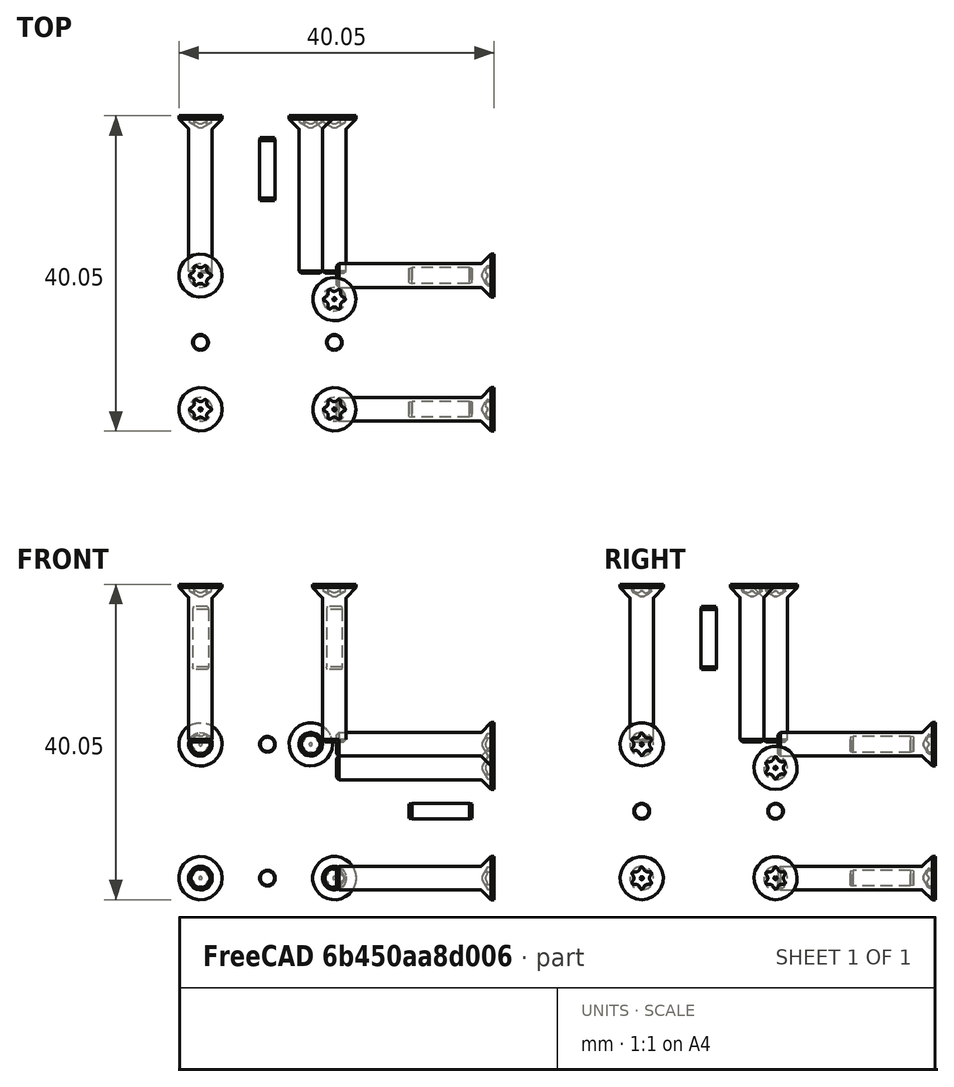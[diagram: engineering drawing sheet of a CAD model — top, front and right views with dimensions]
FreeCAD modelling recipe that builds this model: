
FCSTD DOCUMENT  (FreeCAD 1.2R45225 (Git))
Label: Assembly_MicroManipulator
License: All rights reserved
LicenseURL: https://en.wikipedia.org/wiki/All_rights_reserved
objects: App::Link×125, Part::FeaturePython×18, App::Point×13, Assembly::AssemblyLink×12, App::FeaturePython×4, Assembly::JointGroup×1, App::DocumentObjectGroup×1, Assembly::AssemblyObject×1
note: 18 computed .brp shape members not serialized (recipe doc carries the construction recipe); baked Part::Feature solids carry a one-line shape summary decoded from their .brp
EXTERNAL_REF file=BaseBlock.FCStd obj=Body
EXTERNAL_REF file=EndEffector.FCStd obj=Body
EXTERNAL_REF file=Assembly_Actuator.FCStd obj=Assembly
EXTERNAL_REF file=Assembly_Actuator.FCStd obj=MotorMount
EXTERNAL_REF file=Assembly_Actuator.FCStd obj=StepperMotorNema17
EXTERNAL_REF file=Assembly_Actuator.FCStd obj=MotorHorn
EXTERNAL_REF file=Assembly_Actuator.FCStd obj=LinkageUnit
EXTERNAL_REF file=Assembly_LinkageUnit.FCStd obj=LinkageRod
EXTERNAL_REF file=Assembly_LinkageUnit.FCStd obj=LinkageRod001
EXTERNAL_REF file=Assembly_LinkageUnit.FCStd obj=RubberBandCollet001
EXTERNAL_REF file=Assembly_LinkageUnit.FCStd obj=RubberBandCollet
EXTERNAL_REF file=Assembly_LinkageUnit.FCStd obj=RubberBandCollet002
EXTERNAL_REF file=Assembly_LinkageUnit.FCStd obj=RubberBandCollet003
EXTERNAL_REF file=Assembly_Actuator.FCStd obj=EncoderMAgnetArray
EXTERNAL_REF file=Assembly_Actuator.FCStd obj=MT6835
EXTERNAL_REF file=Assembly_Actuator.FCStd obj=Screw
EXTERNAL_REF file=Assembly_Actuator.FCStd obj=Screw001
EXTERNAL_REF file=Assembly_Actuator.FCStd obj=Screw002
EXTERNAL_REF file=Assembly_Actuator.FCStd obj=Screw003
EXTERNAL_REF file=Assembly_Actuator.FCStd obj=Pin
EXTERNAL_REF file=Assembly_Actuator.FCStd obj=Pin001
EXTERNAL_REF file=Assembly_Actuator.FCStd obj=Screw004
EXTERNAL_REF file=Assembly_Actuator.FCStd obj=Screw005
EXTERNAL_REF file=Assembly_Actuator.FCStd obj=Screw006
EXTERNAL_REF file=Assembly_Actuator.FCStd obj=Pin002
EXTERNAL_REF file=Assembly_Actuator.FCStd obj=Screw007
EXTERNAL_REF file=Assembly_Actuator.FCStd obj=Screw008
EXTERNAL_REF file=Assembly_LinkageUnit.FCStd obj=BallJointPlateAsm
EXTERNAL_REF file=Assembly_BallJointPlate.FCStd obj=BallJointPlate
EXTERNAL_REF file=Assembly_BallJointPlate.FCStd obj=Ball
EXTERNAL_REF file=Assembly_BallJointPlate.FCStd obj=Ball001
EXTERNAL_REF file=Assembly_BallJointPlate.FCStd obj=RubberBand
EXTERNAL_REF file=Assembly_BallJointPlate.FCStd obj=RubberBand001
EXTERNAL_REF file=Assembly_BallJointPlate.FCStd obj=CrimpBead
EXTERNAL_REF file=Assembly_BallJointPlate.FCStd obj=CrimpBead001
EXTERNAL_REF file=Assembly_BallJointPlate.FCStd obj=CrimpBead002
EXTERNAL_REF file=Assembly_BallJointPlate.FCStd obj=CrimpBead003
EXTERNAL_REF file=Assembly_LinkageUnit.FCStd obj=BallJointPlateAsm001

FEATURE [App::Point] Origin001
  Role = Origin
FEATURE [App::Link] BaseBlock
  LinkedObject = -> <external BaseBlock.FCStd>#Body
FEATURE [App::Link] Endeffector
  LinkPlacement = pos=(47.5,47.5,47.5) rot=(0,0,1;0rad)
  LinkedObject = -> <external EndEffector.FCStd>#Body
  Placement = pos=(47.5,47.5,47.5) rot=(0,0,1;0rad)
FEATURE [App::Point] Origin009
  Role = Origin
FEATURE [App::Link] MotorMount
  LinkPlacement = pos=(0,0,-10.5) rot=(0.707107,0.707107,0;3.14159rad)
  LinkedObject = -> <external Assembly_Actuator.FCStd>#MotorMount
  Placement = pos=(0,0,-10.5) rot=(0.707107,0.707107,0;3.14159rad)
FEATURE [App::Link] StepperMotorNema003
  LinkPlacement = pos=(1.13144e-05,-3.1139e-06,-55.5) rot=(0,0,1;1.5708rad)
  LinkedObject = -> <external Assembly_Actuator.FCStd>#StepperMotorNema17
  Placement = pos=(1.13144e-05,-3.1139e-06,-55.5) rot=(0,0,1;1.5708rad)
FEATURE [App::Link] MotorHorn003
  LinkPlacement = pos=(8.34465e-06,1.54972e-05,-10) rot=(0,0,1;0rad)
  LinkedObject = -> <external Assembly_Actuator.FCStd>#MotorHorn
  Placement = pos=(8.34465e-06,1.54972e-05,-10) rot=(0,0,1;0rad)
FEATURE [App::Point] Origin011  label="Origin012"
  Role = Origin
FEATURE [App::Link] LinkageRod  label="LinkageRod1"
  LinkPlacement = pos=(8.5,0,0) rot=(0,0,1;0rad)
  LinkedObject = -> <external Assembly_LinkageUnit.FCStd>#LinkageRod
  Placement = pos=(8.5,0,0) rot=(0,0,1;0rad)
FEATURE [App::Link] LinkageRod001  label="LinkageRod2"
  LinkPlacement = pos=(-8.5,0,0) rot=(0,0,1;0rad)
  LinkedObject = -> <external Assembly_LinkageUnit.FCStd>#LinkageRod001
  Placement = pos=(-8.5,0,0) rot=(0,0,1;0rad)
FEATURE [App::Link] RubberBandCollet012
  LinkPlacement = pos=(-8.5,24.5,5.51344e-07) rot=(0,0.707107,0.707107;3.14159rad)
  LinkedObject = -> <external Assembly_LinkageUnit.FCStd>#RubberBandCollet001
  Placement = pos=(-8.5,24.5,5.51344e-07) rot=(0,0.707107,0.707107;3.14159rad)
FEATURE [App::Link] RubberBandCollet013
  LinkPlacement = pos=(8.5,24.5,4.02331e-07) rot=(0,0.707107,0.707107;3.14159rad)
  LinkedObject = -> <external Assembly_LinkageUnit.FCStd>#RubberBandCollet
  Placement = pos=(8.5,24.5,4.02331e-07) rot=(0,0.707107,0.707107;3.14159rad)
FEATURE [App::Link] RubberBandCollet014
  LinkPlacement = pos=(-8.5,-24.5,-1.1921e-07) rot=(1,0,0;1.5708rad)
  LinkedObject = -> <external Assembly_LinkageUnit.FCStd>#RubberBandCollet002
  Placement = pos=(-8.5,-24.5,-1.1921e-07) rot=(1,0,0;1.5708rad)
FEATURE [App::Link] RubberBandCollet015
  LinkPlacement = pos=(8.5,-24.5,9.98377e-07) rot=(-1,0,0;1.5708rad)
  LinkedObject = -> <external Assembly_LinkageUnit.FCStd>#RubberBandCollet003
  Placement = pos=(8.5,-24.5,9.98377e-07) rot=(-1,0,0;1.5708rad)
FEATURE [App::Link] EncoderMAgnetArray003  label="EncoderMagnetArray"
  LinkPlacement = pos=(9.53674e-07,9.23872e-07,-8.00001) rot=(0,0,1;0rad)
  LinkedObject = -> <external Assembly_Actuator.FCStd>#EncoderMAgnetArray
  Placement = pos=(9.53674e-07,9.23872e-07,-8.00001) rot=(0,0,1;0rad)
FEATURE [App::Link] MT6838
  LinkPlacement = pos=(-32.5,1.41501e-05,-10) rot=(0,1,0;1.5708rad)
  LinkedObject = -> <external Assembly_Actuator.FCStd>#MT6835
  Placement = pos=(-32.5,1.41501e-05,-10) rot=(0,1,0;1.5708rad)
FEATURE [App::Link] Screw  label="M3x10-Screw"
  LinkPlacement = pos=(15.5,15.5,-10.5) rot=(1.0625,0,0;0rad)
  LinkedObject = -> <external Assembly_Actuator.FCStd>#Screw
  Placement = pos=(15.5,15.5,-10.5) rot=(1.0625,0,0;0rad)
FEATURE [App::Link] Screw001  label="M3x10-Screw008"
  LinkPlacement = pos=(-15.5,15.5,-10.5) rot=(1.0625,0,0;0rad)
  LinkedObject = -> <external Assembly_Actuator.FCStd>#Screw001
  Placement = pos=(-15.5,15.5,-10.5) rot=(1.0625,0,0;0rad)
FEATURE [App::Link] Screw002  label="M3x10-Screw009"
  LinkPlacement = pos=(-15.5,-15.5,-10.5) rot=(1.0625,0,0;0rad)
  LinkedObject = -> <external Assembly_Actuator.FCStd>#Screw002
  Placement = pos=(-15.5,-15.5,-10.5) rot=(1.0625,0,0;0rad)
FEATURE [App::Link] Screw003  label="M3x6-Screw"
  LinkPlacement = pos=(15.5,-15.5,-14.5) rot=(1.0625,0,0;0rad)
  LinkedObject = -> <external Assembly_Actuator.FCStd>#Screw003
  Placement = pos=(15.5,-15.5,-14.5) rot=(1.0625,0,0;0rad)
FEATURE [App::Link] Pin  label="2 mmx8-Pin"
  LinkPlacement = pos=(12,0.299999,4.75) rot=(1,0,0;1.5708rad)
  LinkedObject = -> <external Assembly_Actuator.FCStd>#Pin
  Placement = pos=(12,0.299999,4.75) rot=(1,0,0;1.5708rad)
FEATURE [App::Link] Pin001  label="2 mmx8-Pin004"
  LinkPlacement = pos=(12,0.300001,-4.75) rot=(1,0,0;1.5708rad)
  LinkedObject = -> <external Assembly_Actuator.FCStd>#Pin001
  Placement = pos=(12,0.300001,-4.75) rot=(1,0,0;1.5708rad)
FEATURE [App::Link] Screw004  label="M2x8-Screw"
  LinkPlacement = pos=(15,0.299999,4.75) rot=(1,0,0;1.5708rad)
  LinkedObject = -> <external Assembly_Actuator.FCStd>#Screw004
  Placement = pos=(15,0.299999,4.75) rot=(1,0,0;1.5708rad)
FEATURE [App::Link] Screw005  label="M2x8-Screw005"
  LinkPlacement = pos=(15,0.300001,-4.75) rot=(1,0,0;1.5708rad)
  LinkedObject = -> <external Assembly_Actuator.FCStd>#Screw005
  Placement = pos=(15,0.300001,-4.75) rot=(1,0,0;1.5708rad)
FEATURE [App::Link] Screw006  label="M2x8-Screw004"
  LinkPlacement = pos=(-34.1,1.41501e-05,-16) rot=(0,-1,0;1.5708rad)
  LinkedObject = -> <external Assembly_Actuator.FCStd>#Screw006
  Placement = pos=(-34.1,1.41501e-05,-16) rot=(0,-1,0;1.5708rad)
FEATURE [App::FeaturePython] GroundedJoint  # Assembly grounded joint (typed FeaturePython)
  ObjectToGround = -> BaseBlock
FEATURE [App::FeaturePython] Joint  label="Fixed1"  # Assembly joint (typed FeaturePython)
  Angle = 0
  AngleMax = 0
  AngleMin = 0
  Detach1 = false
  Detach2 = false
  Distance = 0
  Distance2 = 0
  EnableAngleMax = false
  EnableAngleMin = false
  EnableLengthMax = false
  EnableLengthMin = false
  JointType = 0 (Fixed)
  LengthMax = 0
  LengthMin = 0
  Offset2 = pos=(-21,-21.5,-52) rot=(0,0,-1;1.5708rad)
  Placement2 = pos=(-21,-21.5,-52) rot=(0,0,-1;1.5708rad)
  Reference1 = -> BaseBlock
  Reference2 = -> Actuator
  Suppressed = false
FEATURE [App::Point] Origin013  label="Origin015"
  Role = Origin
FEATURE [App::Link] MotorMount001
  LinkPlacement = pos=(0,0,-10.5) rot=(0.707107,0.707107,0;3.14159rad)
  LinkedObject = -> <external Assembly_Actuator.FCStd>#MotorMount
  Placement = pos=(0,0,-10.5) rot=(0.707107,0.707107,0;3.14159rad)
FEATURE [App::Link] StepperMotorNema004
  LinkPlacement = pos=(1.13144e-05,-3.1139e-06,-55.5) rot=(0,0,1;1.5708rad)
  LinkedObject = -> <external Assembly_Actuator.FCStd>#StepperMotorNema17
  Placement = pos=(1.13144e-05,-3.1139e-06,-55.5) rot=(0,0,1;1.5708rad)
FEATURE [App::Link] MotorHorn004
  LinkPlacement = pos=(8.34465e-06,1.54972e-05,-10) rot=(0,0,1;0rad)
  LinkedObject = -> <external Assembly_Actuator.FCStd>#MotorHorn
  Placement = pos=(8.34465e-06,1.54972e-05,-10) rot=(0,0,1;0rad)
FEATURE [App::Point] Origin015  label="Origin017"
  Role = Origin
FEATURE [App::Link] LinkageRod002  label="LinkageRod001"
  LinkPlacement = pos=(8.5,0,0) rot=(0,0,1;0rad)
  LinkedObject = -> <external Assembly_LinkageUnit.FCStd>#LinkageRod
  Placement = pos=(8.5,0,0) rot=(0,0,1;0rad)
FEATURE [App::Link] LinkageRod003  label="LinkageRod002"
  LinkPlacement = pos=(-8.5,0,0) rot=(0,0,1;0rad)
  LinkedObject = -> <external Assembly_LinkageUnit.FCStd>#LinkageRod001
  Placement = pos=(-8.5,0,0) rot=(0,0,1;0rad)
FEATURE [App::Link] RubberBandCollet016
  LinkPlacement = pos=(-8.5,24.5,5.51344e-07) rot=(0,0.707107,0.707107;3.14159rad)
  LinkedObject = -> <external Assembly_LinkageUnit.FCStd>#RubberBandCollet001
  Placement = pos=(-8.5,24.5,5.51344e-07) rot=(0,0.707107,0.707107;3.14159rad)
FEATURE [App::Link] RubberBandCollet017
  LinkPlacement = pos=(8.5,24.5,4.02331e-07) rot=(0,0.707107,0.707107;3.14159rad)
  LinkedObject = -> <external Assembly_LinkageUnit.FCStd>#RubberBandCollet
  Placement = pos=(8.5,24.5,4.02331e-07) rot=(0,0.707107,0.707107;3.14159rad)
FEATURE [App::Link] RubberBandCollet018
  LinkPlacement = pos=(-8.5,-24.5,-1.1921e-07) rot=(1,0,0;1.5708rad)
  LinkedObject = -> <external Assembly_LinkageUnit.FCStd>#RubberBandCollet002
  Placement = pos=(-8.5,-24.5,-1.1921e-07) rot=(1,0,0;1.5708rad)
FEATURE [App::Link] RubberBandCollet019
  LinkPlacement = pos=(8.5,-24.5,9.98377e-07) rot=(-1,0,0;1.5708rad)
  LinkedObject = -> <external Assembly_LinkageUnit.FCStd>#RubberBandCollet003
  Placement = pos=(8.5,-24.5,9.98377e-07) rot=(-1,0,0;1.5708rad)
FEATURE [App::Link] EncoderMAgnetArray004  label="EncoderMagnetArray001"
  LinkPlacement = pos=(9.53674e-07,9.23872e-07,-8.00001) rot=(0,0,1;0rad)
  LinkedObject = -> <external Assembly_Actuator.FCStd>#EncoderMAgnetArray
  Placement = pos=(9.53674e-07,9.23872e-07,-8.00001) rot=(0,0,1;0rad)
FEATURE [App::Link] MT6839
  LinkPlacement = pos=(-32.5,1.41501e-05,-10) rot=(0,1,0;1.5708rad)
  LinkedObject = -> <external Assembly_Actuator.FCStd>#MT6835
  Placement = pos=(-32.5,1.41501e-05,-10) rot=(0,1,0;1.5708rad)
FEATURE [App::Link] Screw007  label="M3x10-Screw010"
  LinkPlacement = pos=(15.5,15.5,-10.5) rot=(1.0625,0,0;0rad)
  LinkedObject = -> <external Assembly_Actuator.FCStd>#Screw
  Placement = pos=(15.5,15.5,-10.5) rot=(1.0625,0,0;0rad)
FEATURE [App::Link] Screw008  label="M3x10-Screw011"
  LinkPlacement = pos=(-15.5,15.5,-10.5) rot=(1.0625,0,0;0rad)
  LinkedObject = -> <external Assembly_Actuator.FCStd>#Screw001
  Placement = pos=(-15.5,15.5,-10.5) rot=(1.0625,0,0;0rad)
FEATURE [App::Link] Screw009  label="M3x10-Screw012"
  LinkPlacement = pos=(-15.5,-15.5,-10.5) rot=(1.0625,0,0;0rad)
  LinkedObject = -> <external Assembly_Actuator.FCStd>#Screw002
  Placement = pos=(-15.5,-15.5,-10.5) rot=(1.0625,0,0;0rad)
FEATURE [App::Link] Screw010  label="M3x6-Screw001"
  LinkPlacement = pos=(15.5,-15.5,-14.5) rot=(1.0625,0,0;0rad)
  LinkedObject = -> <external Assembly_Actuator.FCStd>#Screw003
  Placement = pos=(15.5,-15.5,-14.5) rot=(1.0625,0,0;0rad)
FEATURE [App::Link] Pin002  label="2 mmx8-Pin005"
  LinkPlacement = pos=(12,0.299999,4.75) rot=(1,0,0;1.5708rad)
  LinkedObject = -> <external Assembly_Actuator.FCStd>#Pin
  Placement = pos=(12,0.299999,4.75) rot=(1,0,0;1.5708rad)
FEATURE [App::Link] Pin003  label="2 mmx8-Pin006"
  LinkPlacement = pos=(12,0.300001,-4.75) rot=(1,0,0;1.5708rad)
  LinkedObject = -> <external Assembly_Actuator.FCStd>#Pin001
  Placement = pos=(12,0.300001,-4.75) rot=(1,0,0;1.5708rad)
FEATURE [App::Link] Screw011  label="M2x8-Screw006"
  LinkPlacement = pos=(15,0.299999,4.75) rot=(1,0,0;1.5708rad)
  LinkedObject = -> <external Assembly_Actuator.FCStd>#Screw004
  Placement = pos=(15,0.299999,4.75) rot=(1,0,0;1.5708rad)
FEATURE [App::Link] Screw012  label="M2x8-Screw007"
  LinkPlacement = pos=(15,0.300001,-4.75) rot=(1,0,0;1.5708rad)
  LinkedObject = -> <external Assembly_Actuator.FCStd>#Screw005
  Placement = pos=(15,0.300001,-4.75) rot=(1,0,0;1.5708rad)
FEATURE [App::Link] Screw013  label="M2x8-Screw008"
  LinkPlacement = pos=(-34.1,1.41501e-05,-16) rot=(0,-1,0;1.5708rad)
  LinkedObject = -> <external Assembly_Actuator.FCStd>#Screw006
  Placement = pos=(-34.1,1.41501e-05,-16) rot=(0,-1,0;1.5708rad)
FEATURE [App::FeaturePython] Joint001  label="Fixed2"  # Assembly joint (typed FeaturePython)
  Angle = 0
  AngleMax = 0
  AngleMin = 0
  Detach1 = false
  Detach2 = false
  Distance = 0
  Distance2 = 0
  EnableAngleMax = false
  EnableAngleMin = false
  EnableLengthMax = false
  EnableLengthMin = false
  JointType = 0 (Fixed)
  LengthMax = 0
  LengthMin = 0
  Offset2 = pos=(-21,-21.5,-52) rot=(0.707107,0,0.707107;3.14159rad)
  Placement2 = pos=(-21,-21.5,-52) rot=(0.707107,0,0.707107;3.14159rad)
  Reference1 = -> BaseBlock
  Reference2 = -> Actuator001
  Suppressed = false
FEATURE [App::Point] Origin017  label="Origin020"
  Role = Origin
FEATURE [App::Link] MotorMount002
  LinkPlacement = pos=(0,0,-10.5) rot=(0.707107,0.707107,0;3.14159rad)
  LinkedObject = -> <external Assembly_Actuator.FCStd>#MotorMount
  Placement = pos=(0,0,-10.5) rot=(0.707107,0.707107,0;3.14159rad)
FEATURE [App::Link] StepperMotorNema17
  LinkPlacement = pos=(1.13144e-05,-3.1139e-06,-55.5) rot=(0,0,1;1.5708rad)
  LinkedObject = -> <external Assembly_Actuator.FCStd>#StepperMotorNema17
  Placement = pos=(1.13144e-05,-3.1139e-06,-55.5) rot=(0,0,1;1.5708rad)
FEATURE [App::Link] MotorHorn
  LinkPlacement = pos=(8.34465e-06,1.54972e-05,-10) rot=(0,0,1;0rad)
  LinkedObject = -> <external Assembly_Actuator.FCStd>#MotorHorn
  Placement = pos=(8.34465e-06,1.54972e-05,-10) rot=(0,0,1;0rad)
FEATURE [App::Point] Origin019  label="Origin023"
  Role = Origin
FEATURE [App::Link] LinkageRod004  label="LinkageRod003"
  LinkPlacement = pos=(8.5,0,0) rot=(0,0,1;0rad)
  LinkedObject = -> <external Assembly_LinkageUnit.FCStd>#LinkageRod
  Placement = pos=(8.5,0,0) rot=(0,0,1;0rad)
FEATURE [App::Link] LinkageRod005  label="LinkageRod004"
  LinkPlacement = pos=(-8.5,0,0) rot=(0,0,1;0rad)
  LinkedObject = -> <external Assembly_LinkageUnit.FCStd>#LinkageRod001
  Placement = pos=(-8.5,0,0) rot=(0,0,1;0rad)
FEATURE [App::Link] RubberBandCollet001  label="RubberBandCollet1"
  LinkPlacement = pos=(-8.5,24.5,5.51344e-07) rot=(0,0.707107,0.707107;3.14159rad)
  LinkedObject = -> <external Assembly_LinkageUnit.FCStd>#RubberBandCollet001
  Placement = pos=(-8.5,24.5,5.51344e-07) rot=(0,0.707107,0.707107;3.14159rad)
FEATURE [App::Link] RubberBandCollet  label="RubberBandCollet2"
  LinkPlacement = pos=(8.5,24.5,4.02331e-07) rot=(0,0.707107,0.707107;3.14159rad)
  LinkedObject = -> <external Assembly_LinkageUnit.FCStd>#RubberBandCollet
  Placement = pos=(8.5,24.5,4.02331e-07) rot=(0,0.707107,0.707107;3.14159rad)
FEATURE [App::Link] RubberBandCollet002  label="RubberBandCollet3"
  LinkPlacement = pos=(-8.5,-24.5,-1.1921e-07) rot=(1,0,0;1.5708rad)
  LinkedObject = -> <external Assembly_LinkageUnit.FCStd>#RubberBandCollet002
  Placement = pos=(-8.5,-24.5,-1.1921e-07) rot=(1,0,0;1.5708rad)
FEATURE [App::Link] RubberBandCollet003  label="RubberBandCollet4"
  LinkPlacement = pos=(8.5,-24.5,9.98377e-07) rot=(-1,0,0;1.5708rad)
  LinkedObject = -> <external Assembly_LinkageUnit.FCStd>#RubberBandCollet003
  Placement = pos=(8.5,-24.5,9.98377e-07) rot=(-1,0,0;1.5708rad)
FEATURE [App::Link] EncoderMAgnetArray  label="EncoderMagnetArray002"
  LinkPlacement = pos=(9.53674e-07,9.23872e-07,-8.00001) rot=(0,0,1;0rad)
  LinkedObject = -> <external Assembly_Actuator.FCStd>#EncoderMAgnetArray
  Placement = pos=(9.53674e-07,9.23872e-07,-8.00001) rot=(0,0,1;0rad)
FEATURE [App::Link] MT6835
  LinkPlacement = pos=(-32.5,1.41501e-05,-10) rot=(0,1,0;1.5708rad)
  LinkedObject = -> <external Assembly_Actuator.FCStd>#MT6835
  Placement = pos=(-32.5,1.41501e-05,-10) rot=(0,1,0;1.5708rad)
FEATURE [App::Link] Screw014  label="M3x10-Screw013"
  LinkPlacement = pos=(15.5,15.5,-10.5) rot=(1.0625,0,0;0rad)
  LinkedObject = -> <external Assembly_Actuator.FCStd>#Screw
  Placement = pos=(15.5,15.5,-10.5) rot=(1.0625,0,0;0rad)
FEATURE [App::Link] Screw015  label="M3x10-Screw014"
  LinkPlacement = pos=(-15.5,15.5,-10.5) rot=(1.0625,0,0;0rad)
  LinkedObject = -> <external Assembly_Actuator.FCStd>#Screw001
  Placement = pos=(-15.5,15.5,-10.5) rot=(1.0625,0,0;0rad)
FEATURE [App::Link] Screw016  label="M3x10-Screw015"
  LinkPlacement = pos=(-15.5,-15.5,-10.5) rot=(1.0625,0,0;0rad)
  LinkedObject = -> <external Assembly_Actuator.FCStd>#Screw002
  Placement = pos=(-15.5,-15.5,-10.5) rot=(1.0625,0,0;0rad)
FEATURE [App::Link] Screw017  label="M3x6-Screw002"
  LinkPlacement = pos=(15.5,-15.5,-14.5) rot=(1.0625,0,0;0rad)
  LinkedObject = -> <external Assembly_Actuator.FCStd>#Screw003
  Placement = pos=(15.5,-15.5,-14.5) rot=(1.0625,0,0;0rad)
FEATURE [App::Link] Pin004  label="2 mmx8-Pin007"
  LinkPlacement = pos=(12,0.299999,4.75) rot=(1,0,0;1.5708rad)
  LinkedObject = -> <external Assembly_Actuator.FCStd>#Pin
  Placement = pos=(12,0.299999,4.75) rot=(1,0,0;1.5708rad)
FEATURE [App::Link] Pin005  label="2 mmx8-Pin008"
  LinkPlacement = pos=(12,0.300001,-4.75) rot=(1,0,0;1.5708rad)
  LinkedObject = -> <external Assembly_Actuator.FCStd>#Pin001
  Placement = pos=(12,0.300001,-4.75) rot=(1,0,0;1.5708rad)
FEATURE [App::Link] Screw018  label="M2x8-Screw009"
  LinkPlacement = pos=(15,0.299999,4.75) rot=(1,0,0;1.5708rad)
  LinkedObject = -> <external Assembly_Actuator.FCStd>#Screw004
  Placement = pos=(15,0.299999,4.75) rot=(1,0,0;1.5708rad)
FEATURE [App::Link] Screw019  label="M2x8-Screw010"
  LinkPlacement = pos=(15,0.300001,-4.75) rot=(1,0,0;1.5708rad)
  LinkedObject = -> <external Assembly_Actuator.FCStd>#Screw005
  Placement = pos=(15,0.300001,-4.75) rot=(1,0,0;1.5708rad)
FEATURE [App::Link] Screw020  label="M2x8-Screw011"
  LinkPlacement = pos=(-34.1,1.41501e-05,-16) rot=(0,-1,0;1.5708rad)
  LinkedObject = -> <external Assembly_Actuator.FCStd>#Screw006
  Placement = pos=(-34.1,1.41501e-05,-16) rot=(0,-1,0;1.5708rad)
FEATURE [App::FeaturePython] Joint002  label="Fixed3"  # Assembly joint (typed FeaturePython)
  Angle = 0
  AngleMax = 0
  AngleMin = 0
  Detach1 = false
  Detach2 = false
  Distance = 0
  Distance2 = 0
  EnableAngleMax = false
  EnableAngleMin = false
  EnableLengthMax = false
  EnableLengthMin = false
  JointType = 0 (Fixed)
  LengthMax = 0
  LengthMin = 0
  Offset2 = pos=(-21,-21.5,-52) rot=(1,0,0;1.5708rad)
  Placement2 = pos=(-21,-21.5,-52) rot=(1,0,0;1.5708rad)
  Reference1 = -> BaseBlock
  Reference2 = -> Actuator002
  Suppressed = false
FEATURE [Assembly::JointGroup] Joints
  Group = -> [GroundedJoint,Joint,Joint001,Joint002]
FEATURE [Part::FeaturePython] Screw021  label="M3x20-Screw"  # WARN: FeaturePython — macro-defined, semantics opaque (R4)
  BaseObject = -> Actuator [MotorMount.Fillet020.Edge283]
  Diameter = 3
  Invert = false
  LeftHanded = false
  Length = 5
  LengthCustom = 20
  MatchOuter = true
  Offset = -0.2
  OffsetAngle = 0
  Placement = pos=(21,18,41.3) rot=(0,1.0625,0;0rad)
  Thread = false
  Type = 55
FEATURE [Part::FeaturePython] Screw022  label="M3x20-Screw281"  # WARN: FeaturePython — macro-defined, semantics opaque (R4)
  BaseObject = -> Actuator [MotorMount.Fillet020.Edge285]
  Diameter = 3
  Invert = false
  LeftHanded = false
  Length = 5
  LengthCustom = 20
  MatchOuter = true
  Offset = -0.2
  OffsetAngle = 0
  Placement = pos=(4,21,41.3) rot=(0,1.0625,0;0rad)
  Thread = false
  Type = 55
FEATURE [Part::FeaturePython] Screw023  label="M3x20-Screw282"  # WARN: FeaturePython — macro-defined, semantics opaque (R4)
  BaseObject = -> Actuator [MotorMount.Fillet020.Edge260]
  Diameter = 3
  Invert = false
  LeftHanded = false
  Length = 5
  LengthCustom = 20
  MatchOuter = true
  Offset = -0.2
  OffsetAngle = 0
  Placement = pos=(4,4,41.3) rot=(0,1.0625,0;0rad)
  Thread = false
  Type = 55
FEATURE [Part::FeaturePython] Screw024  label="M3x20-Screw283"  # WARN: FeaturePython — macro-defined, semantics opaque (R4)
  BaseObject = -> Actuator [MotorMount.Fillet020.Edge258]
  Diameter = 3
  Invert = false
  LeftHanded = false
  Length = 5
  LengthCustom = 20
  MatchOuter = true
  Offset = -0.2
  OffsetAngle = 0
  Placement = pos=(21,4.00001,41.3) rot=(0,1.0625,0;0rad)
  Thread = false
  Type = 55
FEATURE [Part::FeaturePython] Screw025  label="M3x20-Screw277"  # WARN: FeaturePython — macro-defined, semantics opaque (R4)
  BaseObject = -> Actuator001 [MotorMount001.Fillet020.Edge285]
  Diameter = 3
  Invert = false
  LeftHanded = false
  Length = 5
  LengthCustom = 20
  MatchOuter = true
  Offset = -0.2
  OffsetAngle = 0
  Placement = pos=(41.3,4,21) rot=(0,1,0;1.5708rad)
  Thread = false
  Type = 55
FEATURE [Part::FeaturePython] Screw026  label="M3x20-Screw278"  # WARN: FeaturePython — macro-defined, semantics opaque (R4)
  BaseObject = -> Actuator001 [MotorMount001.Fillet020.Edge283]
  Diameter = 3
  Invert = false
  LeftHanded = false
  Length = 5
  LengthCustom = 20
  MatchOuter = true
  Offset = -0.2
  OffsetAngle = 0
  Placement = pos=(41.3,21,18) rot=(0,1,0;1.5708rad)
  Thread = false
  Type = 55
FEATURE [Part::FeaturePython] Screw027  label="M3x20-Screw279"  # WARN: FeaturePython — macro-defined, semantics opaque (R4)
  BaseObject = -> Actuator001 [MotorMount001.Fillet020.Edge258]
  Diameter = 3
  Invert = false
  LeftHanded = false
  Length = 5
  LengthCustom = 20
  MatchOuter = true
  Offset = -0.2
  OffsetAngle = 0
  Placement = pos=(41.3,21,4.00001) rot=(0,1,0;1.5708rad)
  Thread = false
  Type = 55
FEATURE [Part::FeaturePython] Screw028  label="M3x20-Screw280"  # WARN: FeaturePython — macro-defined, semantics opaque (R4)
  BaseObject = -> Actuator001 [MotorMount001.Fillet020.Edge260]
  Diameter = 3
  Invert = false
  LeftHanded = false
  Length = 5
  LengthCustom = 20
  MatchOuter = true
  Offset = -0.2
  OffsetAngle = 0
  Placement = pos=(41.3,4,4) rot=(0,1,0;1.5708rad)
  Thread = false
  Type = 55
FEATURE [Part::FeaturePython] Screw029  label="M3x20-Screw262"  # WARN: FeaturePython — macro-defined, semantics opaque (R4)
  BaseObject = -> Actuator002 [MotorMount002.Fillet020.Edge260]
  Diameter = 3
  Invert = false
  LeftHanded = false
  Length = 5
  LengthCustom = 20
  MatchOuter = true
  Offset = -0.2
  OffsetAngle = 0
  Placement = pos=(4,41.3,4) rot=(-1,0,0;1.5708rad)
  Thread = false
  Type = 55
FEATURE [Part::FeaturePython] Screw030  label="M3x20-Screw263"  # WARN: FeaturePython — macro-defined, semantics opaque (R4)
  BaseObject = -> Actuator002 [MotorMount002.Fillet020.Edge285]
  Diameter = 3
  Invert = false
  LeftHanded = false
  Length = 5
  LengthCustom = 20
  MatchOuter = true
  Offset = -0.2
  OffsetAngle = 0
  Placement = pos=(21,41.3,4) rot=(-1,0,0;1.5708rad)
  Thread = false
  Type = 55
FEATURE [Part::FeaturePython] Screw031  label="M3x20-Screw264"  # WARN: FeaturePython — macro-defined, semantics opaque (R4)
  BaseObject = -> Actuator002 [MotorMount002.Fillet020.Edge283]
  Diameter = 3
  Invert = false
  LeftHanded = false
  Length = 5
  LengthCustom = 20
  MatchOuter = true
  Offset = -0.2
  OffsetAngle = 0
  Placement = pos=(18,41.3,21) rot=(-1,0,0;1.5708rad)
  Thread = false
  Type = 55
FEATURE [Part::FeaturePython] Screw032  label="M3x20-Screw265"  # WARN: FeaturePython — macro-defined, semantics opaque (R4)
  BaseObject = -> Actuator002 [MotorMount002.Fillet020.Edge258]
  Diameter = 3
  Invert = false
  LeftHanded = false
  Length = 5
  LengthCustom = 20
  MatchOuter = true
  Offset = -0.2
  OffsetAngle = 0
  Placement = pos=(4.00001,41.3,21) rot=(-1,0,0;1.5708rad)
  Thread = false
  Type = 55
FEATURE [Part::FeaturePython] Pin006  label="2 mmx8-Pin027"  # WARN: FeaturePython — macro-defined, semantics opaque (R4)
  BaseObject = -> BaseBlock [Pocket003.Edge15]
  Diameter = 3
  Invert = false
  LeftHanded = false
  Length = 2
  LengthCustom = 8
  Offset = 4
  OffsetAngle = 0
  Placement = pos=(21,12.5,38.5) rot=(0,0,1;0rad)
  Thread = false
  Type = 9
FEATURE [Part::FeaturePython] Pin007  label="2 mmx8-Pin028"  # WARN: FeaturePython — macro-defined, semantics opaque (R4)
  BaseObject = -> BaseBlock [Pocket003.Edge12]
  Diameter = 3
  Invert = false
  LeftHanded = false
  Length = 2
  LengthCustom = 8
  Offset = 4
  OffsetAngle = 0
  Placement = pos=(4,12.5,38.5) rot=(0,0,1;0rad)
  Thread = false
  Type = 9
FEATURE [Part::FeaturePython] Pin008  label="2 mmx8-Pin029"  # WARN: FeaturePython — macro-defined, semantics opaque (R4)
  BaseObject = -> BaseBlock [Pocket003.Edge97]
  Diameter = 3
  Invert = false
  LeftHanded = false
  Length = 2
  LengthCustom = 8
  Offset = 4
  OffsetAngle = 0
  Placement = pos=(38.5,21,12.5) rot=(0,1,0;1.5708rad)
  Thread = false
  Type = 9
FEATURE [Part::FeaturePython] Pin009  label="2 mmx8-Pin030"  # WARN: FeaturePython — macro-defined, semantics opaque (R4)
  BaseObject = -> BaseBlock [Pocket003.Edge94]
  Diameter = 3
  Invert = false
  LeftHanded = false
  Length = 2
  LengthCustom = 8
  Offset = 4
  OffsetAngle = 0
  Placement = pos=(38.5,4,12.5) rot=(0,1,0;1.5708rad)
  Thread = false
  Type = 9
FEATURE [Part::FeaturePython] Pin010  label="2 mmx8-Pin031"  # WARN: FeaturePython — macro-defined, semantics opaque (R4)
  BaseObject = -> BaseBlock [Pocket003.Edge78]
  Diameter = 3
  Invert = false
  LeftHanded = false
  Length = 2
  LengthCustom = 8
  Offset = 4
  OffsetAngle = 0
  Placement = pos=(12.5,38.5,4) rot=(-1,0,0;1.5708rad)
  Thread = false
  Type = 9
FEATURE [Part::FeaturePython] Pin011  label="2 mmx8-Pin032"  # WARN: FeaturePython — macro-defined, semantics opaque (R4)
  BaseObject = -> BaseBlock [Pocket003.Edge74]
  Diameter = 3
  Invert = false
  LeftHanded = false
  Length = 2
  LengthCustom = 8
  Offset = 4
  OffsetAngle = 0
  Placement = pos=(12.5,38.5,21) rot=(-1,0,0;1.5708rad)
  Thread = false
  Type = 9
FEATURE [App::DocumentObjectGroup] Group  label="Fasteners"
  Group = -> [Screw021,Screw022,Screw023,Screw024,Screw025,Screw026,Screw027,Screw028,Screw029,Screw030,Screw031,Screw032,Pin006,Pin007,Pin008,Pin009,Pin010,Pin011]
FEATURE [App::Link] Pin012  label="2 mmx8-Pin009"
  LinkPlacement = pos=(-13,1.54972e-05,-3.75001) rot=(0,0,1;0rad)
  LinkedObject = -> <external Assembly_Actuator.FCStd>#Pin002
  Placement = pos=(-13,1.54972e-05,-3.75001) rot=(0,0,1;0rad)
FEATURE [App::Link] Pin013  label="2 mmx8-Pin033"
  LinkPlacement = pos=(-13,1.54972e-05,-3.75001) rot=(0,0,1;0rad)
  LinkedObject = -> <external Assembly_Actuator.FCStd>#Pin002
  Placement = pos=(-13,1.54972e-05,-3.75001) rot=(0,0,1;0rad)
FEATURE [App::Link] Pin014  label="2 mmx8-Pin034"
  LinkPlacement = pos=(-13,1.54972e-05,-3.75001) rot=(0,0,1;0rad)
  LinkedObject = -> <external Assembly_Actuator.FCStd>#Pin002
  Placement = pos=(-13,1.54972e-05,-3.75001) rot=(0,0,1;0rad)
FEATURE [App::Link] Screw033  label="M3x6-Screw003"
  LinkPlacement = pos=(8.34465e-06,7.90002,1.99999) rot=(-1,0,0;1.5708rad)
  LinkedObject = -> <external Assembly_Actuator.FCStd>#Screw007
  Placement = pos=(8.34465e-06,7.90002,1.99999) rot=(-1,0,0;1.5708rad)
FEATURE [App::Link] Screw034  label="M3x6-Screw004"
  LinkPlacement = pos=(8.34465e-06,7.90002,-7.00001) rot=(-1,0,0;1.5708rad)
  LinkedObject = -> <external Assembly_Actuator.FCStd>#Screw008
  Placement = pos=(8.34465e-06,7.90002,-7.00001) rot=(-1,0,0;1.5708rad)
FEATURE [App::Link] Screw035  label="M3x6-Screw005"
  LinkPlacement = pos=(8.34465e-06,7.90002,1.99999) rot=(-1,0,0;1.5708rad)
  LinkedObject = -> <external Assembly_Actuator.FCStd>#Screw007
  Placement = pos=(8.34465e-06,7.90002,1.99999) rot=(-1,0,0;1.5708rad)
FEATURE [App::Link] Screw036  label="M3x6-Screw006"
  LinkPlacement = pos=(8.34465e-06,7.90002,-7.00001) rot=(-1,0,0;1.5708rad)
  LinkedObject = -> <external Assembly_Actuator.FCStd>#Screw008
  Placement = pos=(8.34465e-06,7.90002,-7.00001) rot=(-1,0,0;1.5708rad)
FEATURE [App::Link] Screw037  label="M3x6-Screw007"
  LinkPlacement = pos=(8.34465e-06,7.90002,1.99999) rot=(-1,0,0;1.5708rad)
  LinkedObject = -> <external Assembly_Actuator.FCStd>#Screw007
  Placement = pos=(8.34465e-06,7.90002,1.99999) rot=(-1,0,0;1.5708rad)
FEATURE [App::Link] Screw038  label="M3x6-Screw008"
  LinkPlacement = pos=(8.34465e-06,7.90002,-7.00001) rot=(-1,0,0;1.5708rad)
  LinkedObject = -> <external Assembly_Actuator.FCStd>#Screw008
  Placement = pos=(8.34465e-06,7.90002,-7.00001) rot=(-1,0,0;1.5708rad)
FEATURE [App::Point] Origin021  label="Origin026"
  Role = Origin
FEATURE [App::Link] BallJointPlate
  LinkPlacement = pos=(0,0,-1.9) rot=(0,0,1;0rad)
  LinkedObject = -> <external Assembly_BallJointPlate.FCStd>#BallJointPlate
  Placement = pos=(0,0,-1.9) rot=(0,0,1;0rad)
FEATURE [App::Link] Ball  label="Ball1"
  LinkPlacement = pos=(8.5,0,0) rot=(0,0,1;0rad)
  LinkedObject = -> <external Assembly_BallJointPlate.FCStd>#Ball
  Placement = pos=(8.5,0,0) rot=(0,0,1;0rad)
FEATURE [App::Link] Ball001  label="Ball2"
  LinkPlacement = pos=(-8.5,0,0) rot=(0,0,1;0rad)
  LinkedObject = -> <external Assembly_BallJointPlate.FCStd>#Ball001
  Placement = pos=(-8.5,0,0) rot=(0,0,1;0rad)
FEATURE [App::Link] RubberBand008  label="RubberBand005"
  LinkPlacement = pos=(8.5,0,13.35) rot=(-0.57735,0.57735,0.57735;4.18879rad)
  LinkedObject = -> <external Assembly_BallJointPlate.FCStd>#RubberBand
  Placement = pos=(8.5,0,13.35) rot=(-0.57735,0.57735,0.57735;4.18879rad)
FEATURE [App::Link] RubberBand009  label="RubberBand006"
  LinkPlacement = pos=(-8.5,0,13.35) rot=(0.57735,0.57735,0.57735;2.0944rad)
  LinkedObject = -> <external Assembly_BallJointPlate.FCStd>#RubberBand001
  Placement = pos=(-8.5,0,13.35) rot=(0.57735,0.57735,0.57735;2.0944rad)
FEATURE [App::Link] CrimpBead  label="CrimpBead1a"
  LinkPlacement = pos=(8.5,1.75,-2.4) rot=(0,0,1;1.5708rad)
  LinkedObject = -> <external Assembly_BallJointPlate.FCStd>#CrimpBead
  Placement = pos=(8.5,1.75,-2.4) rot=(0,0,1;1.5708rad)
FEATURE [App::Link] CrimpBead001  label="CrimpBead1b"
  LinkPlacement = pos=(8.5,-1.75,-2.4) rot=(0,0,1;1.5708rad)
  LinkedObject = -> <external Assembly_BallJointPlate.FCStd>#CrimpBead001
  Placement = pos=(8.5,-1.75,-2.4) rot=(0,0,1;1.5708rad)
FEATURE [App::Link] CrimpBead002  label="CrimpBead2a"
  LinkPlacement = pos=(-8.5,1.75,-2.4) rot=(0,0,-1;1.5708rad)
  LinkedObject = -> <external Assembly_BallJointPlate.FCStd>#CrimpBead002
  Placement = pos=(-8.5,1.75,-2.4) rot=(0,0,-1;1.5708rad)
FEATURE [App::Link] CrimpBead003  label="CrimpBead2b"
  LinkPlacement = pos=(-8.5,-1.75,-2.4) rot=(0,0,-1;1.5708rad)
  LinkedObject = -> <external Assembly_BallJointPlate.FCStd>#CrimpBead003
  Placement = pos=(-8.5,-1.75,-2.4) rot=(0,0,-1;1.5708rad)
FEATURE [Assembly::AssemblyLink] BallJointPlateAsm
  Group = -> [BallJointPlate,Ball,Ball001,RubberBand008,RubberBand009,CrimpBead,CrimpBead001,CrimpBead002,CrimpBead003]
  LinkedObject = -> <external Assembly_LinkageUnit.FCStd>#BallJointPlateAsm
  Origin = -> Origin020
  Placement = pos=(0,36.25,0) rot=(1,0,0;1.5708rad)
  Rigid = true
FEATURE [App::Point] Origin023  label="Origin028"
  Role = Origin
FEATURE [App::Link] BallJointPlate010
  LinkPlacement = pos=(0,0,-1.9) rot=(0,0,1;0rad)
  LinkedObject = -> <external Assembly_BallJointPlate.FCStd>#BallJointPlate
  Placement = pos=(0,0,-1.9) rot=(0,0,1;0rad)
FEATURE [App::Link] Ball020
  LinkPlacement = pos=(8.5,0,0) rot=(0,0,1;0rad)
  LinkedObject = -> <external Assembly_BallJointPlate.FCStd>#Ball
  Placement = pos=(8.5,0,0) rot=(0,0,1;0rad)
FEATURE [App::Link] Ball021
  LinkPlacement = pos=(-8.5,0,0) rot=(0,0,1;0rad)
  LinkedObject = -> <external Assembly_BallJointPlate.FCStd>#Ball001
  Placement = pos=(-8.5,0,0) rot=(0,0,1;0rad)
FEATURE [App::Link] RubberBand010  label="RubberBand007"
  LinkPlacement = pos=(8.5,0,13.35) rot=(-0.57735,0.57735,0.57735;4.18879rad)
  LinkedObject = -> <external Assembly_BallJointPlate.FCStd>#RubberBand
  Placement = pos=(8.5,0,13.35) rot=(-0.57735,0.57735,0.57735;4.18879rad)
FEATURE [App::Link] RubberBand011  label="RubberBand008"
  LinkPlacement = pos=(-8.5,0,13.35) rot=(0.57735,0.57735,0.57735;2.0944rad)
  LinkedObject = -> <external Assembly_BallJointPlate.FCStd>#RubberBand001
  Placement = pos=(-8.5,0,13.35) rot=(0.57735,0.57735,0.57735;2.0944rad)
FEATURE [App::Link] CrimpBead004  label="CrimpBead1a001"
  LinkPlacement = pos=(8.5,1.75,-2.4) rot=(0,0,1;1.5708rad)
  LinkedObject = -> <external Assembly_BallJointPlate.FCStd>#CrimpBead
  Placement = pos=(8.5,1.75,-2.4) rot=(0,0,1;1.5708rad)
FEATURE [App::Link] CrimpBead005  label="CrimpBead1b001"
  LinkPlacement = pos=(8.5,-1.75,-2.4) rot=(0,0,1;1.5708rad)
  LinkedObject = -> <external Assembly_BallJointPlate.FCStd>#CrimpBead001
  Placement = pos=(8.5,-1.75,-2.4) rot=(0,0,1;1.5708rad)
FEATURE [App::Link] CrimpBead006  label="CrimpBead2a001"
  LinkPlacement = pos=(-8.5,1.75,-2.4) rot=(0,0,-1;1.5708rad)
  LinkedObject = -> <external Assembly_BallJointPlate.FCStd>#CrimpBead002
  Placement = pos=(-8.5,1.75,-2.4) rot=(0,0,-1;1.5708rad)
FEATURE [App::Link] CrimpBead007  label="CrimpBead2b001"
  LinkPlacement = pos=(-8.5,-1.75,-2.4) rot=(0,0,-1;1.5708rad)
  LinkedObject = -> <external Assembly_BallJointPlate.FCStd>#CrimpBead003
  Placement = pos=(-8.5,-1.75,-2.4) rot=(0,0,-1;1.5708rad)
FEATURE [Assembly::AssemblyLink] BallJointPlateAsm001  label="BallJointPlateAsm"
  Group = -> [BallJointPlate010,Ball020,Ball021,RubberBand010,RubberBand011,CrimpBead004,CrimpBead005,CrimpBead006,CrimpBead007]
  LinkedObject = -> <external Assembly_LinkageUnit.FCStd>#BallJointPlateAsm001
  Origin = -> Origin022
  Placement = pos=(0,-36.25,0) rot=(0,0.707107,0.707107;3.14159rad)
  Rigid = true
FEATURE [Assembly::AssemblyLink] LinkageUnit002  label="LinkageUnit"
  Group = -> [LinkageRod004,LinkageRod005,RubberBandCollet001,RubberBandCollet,RubberBandCollet002,RubberBandCollet003,BallJointPlateAsm,BallJointPlateAsm001]
  LinkedObject = -> <external Assembly_Actuator.FCStd>#LinkageUnit
  Origin = -> Origin018
  Placement = pos=(15,-36.25,-9.53674e-07) rot=(0,1,0;1.5708rad)
  Rigid = true
FEATURE [Assembly::AssemblyLink] Actuator002  label="Actuator3"
  Group = -> [MotorMount002,StepperMotorNema17,MotorHorn,LinkageUnit002,EncoderMAgnetArray,MT6835,Screw014,Screw015,Screw016,Screw017,Pin004,Pin005,Screw018,Screw019,Screw020,Pin014,Screw037,Screw038]
  LinkedObject = -> <external Assembly_Actuator.FCStd>#Assembly
  Origin = -> Origin016
  Placement = pos=(21,52,-21.5) rot=(-1,0,0;1.5708rad)
  Rigid = true
FEATURE [App::Point] Origin025  label="Origin031"
  Role = Origin
FEATURE [App::Link] BallJointPlate011
  LinkPlacement = pos=(0,0,-1.9) rot=(0,0,1;0rad)
  LinkedObject = -> <external Assembly_BallJointPlate.FCStd>#BallJointPlate
  Placement = pos=(0,0,-1.9) rot=(0,0,1;0rad)
FEATURE [App::Link] Ball022
  LinkPlacement = pos=(8.5,0,0) rot=(0,0,1;0rad)
  LinkedObject = -> <external Assembly_BallJointPlate.FCStd>#Ball
  Placement = pos=(8.5,0,0) rot=(0,0,1;0rad)
FEATURE [App::Link] Ball023
  LinkPlacement = pos=(-8.5,0,0) rot=(0,0,1;0rad)
  LinkedObject = -> <external Assembly_BallJointPlate.FCStd>#Ball001
  Placement = pos=(-8.5,0,0) rot=(0,0,1;0rad)
FEATURE [App::Link] RubberBand012  label="RubberBand009"
  LinkPlacement = pos=(8.5,0,13.35) rot=(-0.57735,0.57735,0.57735;4.18879rad)
  LinkedObject = -> <external Assembly_BallJointPlate.FCStd>#RubberBand
  Placement = pos=(8.5,0,13.35) rot=(-0.57735,0.57735,0.57735;4.18879rad)
FEATURE [App::Link] RubberBand013  label="RubberBand010"
  LinkPlacement = pos=(-8.5,0,13.35) rot=(0.57735,0.57735,0.57735;2.0944rad)
  LinkedObject = -> <external Assembly_BallJointPlate.FCStd>#RubberBand001
  Placement = pos=(-8.5,0,13.35) rot=(0.57735,0.57735,0.57735;2.0944rad)
FEATURE [App::Link] CrimpBead008  label="CrimpBead1a002"
  LinkPlacement = pos=(8.5,1.75,-2.4) rot=(0,0,1;1.5708rad)
  LinkedObject = -> <external Assembly_BallJointPlate.FCStd>#CrimpBead
  Placement = pos=(8.5,1.75,-2.4) rot=(0,0,1;1.5708rad)
FEATURE [App::Link] CrimpBead009  label="CrimpBead1b002"
  LinkPlacement = pos=(8.5,-1.75,-2.4) rot=(0,0,1;1.5708rad)
  LinkedObject = -> <external Assembly_BallJointPlate.FCStd>#CrimpBead001
  Placement = pos=(8.5,-1.75,-2.4) rot=(0,0,1;1.5708rad)
FEATURE [App::Link] CrimpBead010  label="CrimpBead2a002"
  LinkPlacement = pos=(-8.5,1.75,-2.4) rot=(0,0,-1;1.5708rad)
  LinkedObject = -> <external Assembly_BallJointPlate.FCStd>#CrimpBead002
  Placement = pos=(-8.5,1.75,-2.4) rot=(0,0,-1;1.5708rad)
FEATURE [App::Link] CrimpBead011  label="CrimpBead2b002"
  LinkPlacement = pos=(-8.5,-1.75,-2.4) rot=(0,0,-1;1.5708rad)
  LinkedObject = -> <external Assembly_BallJointPlate.FCStd>#CrimpBead003
  Placement = pos=(-8.5,-1.75,-2.4) rot=(0,0,-1;1.5708rad)
FEATURE [Assembly::AssemblyLink] BallJointPlateAsm002  label="BallJointPlateAsm"
  Group = -> [BallJointPlate011,Ball022,Ball023,RubberBand012,RubberBand013,CrimpBead008,CrimpBead009,CrimpBead010,CrimpBead011]
  LinkedObject = -> <external Assembly_LinkageUnit.FCStd>#BallJointPlateAsm
  Origin = -> Origin024
  Placement = pos=(0,36.25,0) rot=(1,0,0;1.5708rad)
  Rigid = true
FEATURE [App::Point] Origin027  label="Origin034"
  Role = Origin
FEATURE [App::Link] BallJointPlate012
  LinkPlacement = pos=(0,0,-1.9) rot=(0,0,1;0rad)
  LinkedObject = -> <external Assembly_BallJointPlate.FCStd>#BallJointPlate
  Placement = pos=(0,0,-1.9) rot=(0,0,1;0rad)
FEATURE [App::Link] Ball024
  LinkPlacement = pos=(8.5,0,0) rot=(0,0,1;0rad)
  LinkedObject = -> <external Assembly_BallJointPlate.FCStd>#Ball
  Placement = pos=(8.5,0,0) rot=(0,0,1;0rad)
FEATURE [App::Link] Ball025
  LinkPlacement = pos=(-8.5,0,0) rot=(0,0,1;0rad)
  LinkedObject = -> <external Assembly_BallJointPlate.FCStd>#Ball001
  Placement = pos=(-8.5,0,0) rot=(0,0,1;0rad)
FEATURE [App::Link] RubberBand014  label="RubberBand011"
  LinkPlacement = pos=(8.5,0,13.35) rot=(-0.57735,0.57735,0.57735;4.18879rad)
  LinkedObject = -> <external Assembly_BallJointPlate.FCStd>#RubberBand
  Placement = pos=(8.5,0,13.35) rot=(-0.57735,0.57735,0.57735;4.18879rad)
FEATURE [App::Link] RubberBand015  label="RubberBand012"
  LinkPlacement = pos=(-8.5,0,13.35) rot=(0.57735,0.57735,0.57735;2.0944rad)
  LinkedObject = -> <external Assembly_BallJointPlate.FCStd>#RubberBand001
  Placement = pos=(-8.5,0,13.35) rot=(0.57735,0.57735,0.57735;2.0944rad)
FEATURE [App::Link] CrimpBead012  label="CrimpBead1a003"
  LinkPlacement = pos=(8.5,1.75,-2.4) rot=(0,0,1;1.5708rad)
  LinkedObject = -> <external Assembly_BallJointPlate.FCStd>#CrimpBead
  Placement = pos=(8.5,1.75,-2.4) rot=(0,0,1;1.5708rad)
FEATURE [App::Link] CrimpBead013  label="CrimpBead1b003"
  LinkPlacement = pos=(8.5,-1.75,-2.4) rot=(0,0,1;1.5708rad)
  LinkedObject = -> <external Assembly_BallJointPlate.FCStd>#CrimpBead001
  Placement = pos=(8.5,-1.75,-2.4) rot=(0,0,1;1.5708rad)
FEATURE [App::Link] CrimpBead014  label="CrimpBead2a003"
  LinkPlacement = pos=(-8.5,1.75,-2.4) rot=(0,0,-1;1.5708rad)
  LinkedObject = -> <external Assembly_BallJointPlate.FCStd>#CrimpBead002
  Placement = pos=(-8.5,1.75,-2.4) rot=(0,0,-1;1.5708rad)
FEATURE [App::Link] CrimpBead015  label="CrimpBead2b003"
  LinkPlacement = pos=(-8.5,-1.75,-2.4) rot=(0,0,-1;1.5708rad)
  LinkedObject = -> <external Assembly_BallJointPlate.FCStd>#CrimpBead003
  Placement = pos=(-8.5,-1.75,-2.4) rot=(0,0,-1;1.5708rad)
FEATURE [Assembly::AssemblyLink] BallJointPlateAsm003  label="BallJointPlateAsm"
  Group = -> [BallJointPlate012,Ball024,Ball025,RubberBand014,RubberBand015,CrimpBead012,CrimpBead013,CrimpBead014,CrimpBead015]
  LinkedObject = -> <external Assembly_LinkageUnit.FCStd>#BallJointPlateAsm001
  Origin = -> Origin026
  Placement = pos=(0,-36.25,0) rot=(0,0.707107,0.707107;3.14159rad)
  Rigid = true
FEATURE [Assembly::AssemblyLink] LinkageUnit001  label="LinkageUnit"
  Group = -> [LinkageRod002,LinkageRod003,RubberBandCollet016,RubberBandCollet017,RubberBandCollet018,RubberBandCollet019,BallJointPlateAsm002,BallJointPlateAsm003]
  LinkedObject = -> <external Assembly_Actuator.FCStd>#LinkageUnit
  Origin = -> Origin014
  Placement = pos=(15,-36.25,-9.53674e-07) rot=(0,1,0;1.5708rad)
  Rigid = true
FEATURE [Assembly::AssemblyLink] Actuator001  label="Actuator2"
  Group = -> [MotorMount001,StepperMotorNema004,MotorHorn004,LinkageUnit001,EncoderMAgnetArray004,MT6839,Screw007,Screw008,Screw009,Screw010,Pin002,Pin003,Screw011,Screw012,Screw013,Pin013,Screw035,Screw036]
  LinkedObject = -> <external Assembly_Actuator.FCStd>#Assembly
  Origin = -> Origin012
  Placement = pos=(52,-21.5,21) rot=(0.707107,0,0.707107;3.14159rad)
  Rigid = true
FEATURE [App::Point] Origin029  label="Origin037"
  Role = Origin
FEATURE [App::Link] BallJointPlate013
  LinkPlacement = pos=(0,0,-1.9) rot=(0,0,1;0rad)
  LinkedObject = -> <external Assembly_BallJointPlate.FCStd>#BallJointPlate
  Placement = pos=(0,0,-1.9) rot=(0,0,1;0rad)
FEATURE [App::Link] Ball026
  LinkPlacement = pos=(8.5,0,0) rot=(0,0,1;0rad)
  LinkedObject = -> <external Assembly_BallJointPlate.FCStd>#Ball
  Placement = pos=(8.5,0,0) rot=(0,0,1;0rad)
FEATURE [App::Link] Ball027
  LinkPlacement = pos=(-8.5,0,0) rot=(0,0,1;0rad)
  LinkedObject = -> <external Assembly_BallJointPlate.FCStd>#Ball001
  Placement = pos=(-8.5,0,0) rot=(0,0,1;0rad)
FEATURE [App::Link] RubberBand  label="RubberBand1"
  LinkPlacement = pos=(8.5,0,13.35) rot=(-0.57735,0.57735,0.57735;4.18879rad)
  LinkedObject = -> <external Assembly_BallJointPlate.FCStd>#RubberBand
  Placement = pos=(8.5,0,13.35) rot=(-0.57735,0.57735,0.57735;4.18879rad)
FEATURE [App::Link] RubberBand001  label="RubberBand2"
  LinkPlacement = pos=(-8.5,0,13.35) rot=(0.57735,0.57735,0.57735;2.0944rad)
  LinkedObject = -> <external Assembly_BallJointPlate.FCStd>#RubberBand001
  Placement = pos=(-8.5,0,13.35) rot=(0.57735,0.57735,0.57735;2.0944rad)
FEATURE [App::Link] CrimpBead016  label="CrimpBead1a004"
  LinkPlacement = pos=(8.5,1.75,-2.4) rot=(0,0,1;1.5708rad)
  LinkedObject = -> <external Assembly_BallJointPlate.FCStd>#CrimpBead
  Placement = pos=(8.5,1.75,-2.4) rot=(0,0,1;1.5708rad)
FEATURE [App::Link] CrimpBead017  label="CrimpBead1b004"
  LinkPlacement = pos=(8.5,-1.75,-2.4) rot=(0,0,1;1.5708rad)
  LinkedObject = -> <external Assembly_BallJointPlate.FCStd>#CrimpBead001
  Placement = pos=(8.5,-1.75,-2.4) rot=(0,0,1;1.5708rad)
FEATURE [App::Link] CrimpBead018  label="CrimpBead2a004"
  LinkPlacement = pos=(-8.5,1.75,-2.4) rot=(0,0,-1;1.5708rad)
  LinkedObject = -> <external Assembly_BallJointPlate.FCStd>#CrimpBead002
  Placement = pos=(-8.5,1.75,-2.4) rot=(0,0,-1;1.5708rad)
FEATURE [App::Link] CrimpBead019  label="CrimpBead2b004"
  LinkPlacement = pos=(-8.5,-1.75,-2.4) rot=(0,0,-1;1.5708rad)
  LinkedObject = -> <external Assembly_BallJointPlate.FCStd>#CrimpBead003
  Placement = pos=(-8.5,-1.75,-2.4) rot=(0,0,-1;1.5708rad)
FEATURE [Assembly::AssemblyLink] BallJointPlateAsm004  label="BallJointPlateAsm"
  Group = -> [BallJointPlate013,Ball026,Ball027,RubberBand,RubberBand001,CrimpBead016,CrimpBead017,CrimpBead018,CrimpBead019]
  LinkedObject = -> <external Assembly_LinkageUnit.FCStd>#BallJointPlateAsm
  Origin = -> Origin028
  Placement = pos=(0,36.25,0) rot=(1,0,0;1.5708rad)
  Rigid = true
FEATURE [App::Point] Origin031  label="Origin039"
  Role = Origin
FEATURE [App::Link] BallJointPlate014
  LinkPlacement = pos=(0,0,-1.9) rot=(0,0,1;0rad)
  LinkedObject = -> <external Assembly_BallJointPlate.FCStd>#BallJointPlate
  Placement = pos=(0,0,-1.9) rot=(0,0,1;0rad)
FEATURE [App::Link] Ball028
  LinkPlacement = pos=(8.5,0,0) rot=(0,0,1;0rad)
  LinkedObject = -> <external Assembly_BallJointPlate.FCStd>#Ball
  Placement = pos=(8.5,0,0) rot=(0,0,1;0rad)
FEATURE [App::Link] Ball029
  LinkPlacement = pos=(-8.5,0,0) rot=(0,0,1;0rad)
  LinkedObject = -> <external Assembly_BallJointPlate.FCStd>#Ball001
  Placement = pos=(-8.5,0,0) rot=(0,0,1;0rad)
FEATURE [App::Link] RubberBand016  label="RubberBand013"
  LinkPlacement = pos=(8.5,0,13.35) rot=(-0.57735,0.57735,0.57735;4.18879rad)
  LinkedObject = -> <external Assembly_BallJointPlate.FCStd>#RubberBand
  Placement = pos=(8.5,0,13.35) rot=(-0.57735,0.57735,0.57735;4.18879rad)
FEATURE [App::Link] RubberBand017  label="RubberBand014"
  LinkPlacement = pos=(-8.5,0,13.35) rot=(0.57735,0.57735,0.57735;2.0944rad)
  LinkedObject = -> <external Assembly_BallJointPlate.FCStd>#RubberBand001
  Placement = pos=(-8.5,0,13.35) rot=(0.57735,0.57735,0.57735;2.0944rad)
FEATURE [App::Link] CrimpBead020  label="CrimpBead1a005"
  LinkPlacement = pos=(8.5,1.75,-2.4) rot=(0,0,1;1.5708rad)
  LinkedObject = -> <external Assembly_BallJointPlate.FCStd>#CrimpBead
  Placement = pos=(8.5,1.75,-2.4) rot=(0,0,1;1.5708rad)
FEATURE [App::Link] CrimpBead021  label="CrimpBead1b005"
  LinkPlacement = pos=(8.5,-1.75,-2.4) rot=(0,0,1;1.5708rad)
  LinkedObject = -> <external Assembly_BallJointPlate.FCStd>#CrimpBead001
  Placement = pos=(8.5,-1.75,-2.4) rot=(0,0,1;1.5708rad)
FEATURE [App::Link] CrimpBead022  label="CrimpBead2a005"
  LinkPlacement = pos=(-8.5,1.75,-2.4) rot=(0,0,-1;1.5708rad)
  LinkedObject = -> <external Assembly_BallJointPlate.FCStd>#CrimpBead002
  Placement = pos=(-8.5,1.75,-2.4) rot=(0,0,-1;1.5708rad)
FEATURE [App::Link] CrimpBead023  label="CrimpBead2b005"
  LinkPlacement = pos=(-8.5,-1.75,-2.4) rot=(0,0,-1;1.5708rad)
  LinkedObject = -> <external Assembly_BallJointPlate.FCStd>#CrimpBead003
  Placement = pos=(-8.5,-1.75,-2.4) rot=(0,0,-1;1.5708rad)
FEATURE [Assembly::AssemblyLink] BallJointPlateAsm005  label="BallJointPlateAsm"
  Group = -> [BallJointPlate014,Ball028,Ball029,RubberBand016,RubberBand017,CrimpBead020,CrimpBead021,CrimpBead022,CrimpBead023]
  LinkedObject = -> <external Assembly_LinkageUnit.FCStd>#BallJointPlateAsm001
  Origin = -> Origin030
  Placement = pos=(0,-36.25,0) rot=(0,0.707107,0.707107;3.14159rad)
  Rigid = true
FEATURE [Assembly::AssemblyLink] LinkageUnit
  Group = -> [LinkageRod,LinkageRod001,RubberBandCollet012,RubberBandCollet013,RubberBandCollet014,RubberBandCollet015,BallJointPlateAsm004,BallJointPlateAsm005]
  LinkedObject = -> <external Assembly_Actuator.FCStd>#LinkageUnit
  Origin = -> Origin010
  Placement = pos=(15,-36.25,-9.53674e-07) rot=(0,1,0;1.5708rad)
  Rigid = true
FEATURE [Assembly::AssemblyLink] Actuator  label="Actuator1"
  Group = -> [MotorMount,StepperMotorNema003,MotorHorn003,LinkageUnit,EncoderMAgnetArray003,MT6838,Screw,Screw001,Screw002,Screw003,Pin,Pin001,Screw004,Screw005,Screw006,Pin012,Screw033,Screw034]
  LinkedObject = -> <external Assembly_Actuator.FCStd>#Assembly
  Origin = -> Origin008
  Placement = pos=(-21.5,21,52) rot=(0,0,1;1.5708rad)
  Rigid = true
FEATURE [Assembly::AssemblyObject] Assembly  label="Assembly_MicroManipulator"
  Group = -> [Joints,BaseBlock,Endeffector,Actuator,GroundedJoint,Joint,Actuator001,Joint001,Actuator002,Joint002,Group,Screw021,Screw022,Screw023,Screw024,Screw025,Screw026,Screw027,Screw028,Screw029,Screw030,Screw031,Screw032,Pin006,Pin007,Pin008,Pin009,Pin010,Pin011]
  Origin = -> Origin
  Type = Assembly

RESOLVED EXTERNAL PARTS (link-assembly join: the EXTERNAL_REF files above that resolve inside this repo's crawl, each included once):
---- part Assembly_Actuator.FCStd = doc fcstd_4d8a858f5061 ----
FCSTD DOCUMENT  (FreeCAD 1.2R45225 (Git))
Label: Assembly_Actuator
License: All rights reserved
LicenseURL: https://en.wikipedia.org/wiki/All_rights_reserved
objects: App::Link×29, Part::FeaturePython×12, App::Point×4, Assembly::AssemblyLink×3, Assembly::JointGroup×1, App::DocumentObjectGroup×1, Assembly::AssemblyObject×1
note: 12 computed .brp shape members not serialized (recipe doc carries the construction recipe); baked Part::Feature solids carry a one-line shape summary decoded from their .brp
EXTERNAL_REF file=MotorHorn.FCStd obj=Body
EXTERNAL_REF file=StepperMotorNema17.FCStd obj=Part
EXTERNAL_REF file=EncoderMagnetArray.FCStd obj=Body
EXTERNAL_REF file=MT6835.FCStd obj=Body
EXTERNAL_REF file=Assembly_LinkageUnit.FCStd obj=Assembly
EXTERNAL_REF file=Assembly_LinkageUnit.FCStd obj=LinkageRod
EXTERNAL_REF file=Assembly_LinkageUnit.FCStd obj=LinkageRod001
EXTERNAL_REF file=Assembly_LinkageUnit.FCStd obj=RubberBandCollet001
EXTERNAL_REF file=Assembly_LinkageUnit.FCStd obj=RubberBandCollet
EXTERNAL_REF file=Assembly_LinkageUnit.FCStd obj=RubberBandCollet002
EXTERNAL_REF file=Assembly_LinkageUnit.FCStd obj=RubberBandCollet003
EXTERNAL_REF file=MotorMount.FCStd obj=Body
EXTERNAL_REF file=Assembly_LinkageUnit.FCStd obj=BallJointPlateAsm
EXTERNAL_REF file=Assembly_BallJointPlate.FCStd obj=BallJointPlate
EXTERNAL_REF file=Assembly_BallJointPlate.FCStd obj=Ball
EXTERNAL_REF file=Assembly_BallJointPlate.FCStd obj=Ball001
EXTERNAL_REF file=Assembly_BallJointPlate.FCStd obj=RubberBand
EXTERNAL_REF file=Assembly_BallJointPlate.FCStd obj=RubberBand001
EXTERNAL_REF file=Assembly_BallJointPlate.FCStd obj=CrimpBead
EXTERNAL_REF file=Assembly_BallJointPlate.FCStd obj=CrimpBead001
EXTERNAL_REF file=Assembly_BallJointPlate.FCStd obj=CrimpBead002
EXTERNAL_REF file=Assembly_BallJointPlate.FCStd obj=CrimpBead003
EXTERNAL_REF file=Assembly_LinkageUnit.FCStd obj=BallJointPlateAsm001

FEATURE [App::Point] Origin001
  Role = Origin
FEATURE [Assembly::JointGroup] Joints
FEATURE [App::Link] MotorHorn
  LinkPlacement = pos=(8.34465e-06,1.54972e-05,-10) rot=(0,0,1;0rad)
  LinkedObject = -> <external MotorHorn.FCStd>#Body
  Placement = pos=(8.34465e-06,1.54972e-05,-10) rot=(0,0,1;0rad)
FEATURE [App::Link] StepperMotorNema17
  LinkPlacement = pos=(1.13144e-05,-3.1139e-06,-55.5) rot=(0,0,1;1.5708rad)
  LinkedObject = -> <external StepperMotorNema17.FCStd>#Part
  Placement = pos=(1.13144e-05,-3.1139e-06,-55.5) rot=(0,0,1;1.5708rad)
FEATURE [App::Link] EncoderMAgnetArray  label="EncoderMagnetArray"
  LinkPlacement = pos=(9.53674e-07,9.23872e-07,-8.00001) rot=(0,0,1;0rad)
  LinkedObject = -> <external EncoderMagnetArray.FCStd>#Body
  Placement = pos=(9.53674e-07,9.23872e-07,-8.00001) rot=(0,0,1;0rad)
FEATURE [App::Link] MT6835
  LinkPlacement = pos=(-32.5,1.41501e-05,-10) rot=(0,1,0;1.5708rad)
  LinkedObject = -> <external MT6835.FCStd>#Body
  Placement = pos=(-32.5,1.41501e-05,-10) rot=(0,1,0;1.5708rad)
FEATURE [App::Point] Origin003
  Role = Origin
FEATURE [App::Link] LinkageRod  label="LinkageRod1"
  LinkPlacement = pos=(8.5,0,0) rot=(0,0,1;0rad)
  LinkedObject = -> <external Assembly_LinkageUnit.FCStd>#LinkageRod
  Placement = pos=(8.5,0,0) rot=(0,0,1;0rad)
FEATURE [App::Link] LinkageRod001  label="LinkageRod2"
  LinkPlacement = pos=(-8.5,0,0) rot=(0,0,1;0rad)
  LinkedObject = -> <external Assembly_LinkageUnit.FCStd>#LinkageRod001
  Placement = pos=(-8.5,0,0) rot=(0,0,1;0rad)
FEATURE [App::Link] RubberBandCollet001  label="RubberBandCollet1"
  LinkPlacement = pos=(-8.5,24.5,5.51344e-07) rot=(0,0.707107,0.707107;3.14159rad)
  LinkedObject = -> <external Assembly_LinkageUnit.FCStd>#RubberBandCollet001
  Placement = pos=(-8.5,24.5,5.51344e-07) rot=(0,0.707107,0.707107;3.14159rad)
FEATURE [App::Link] RubberBandCollet  label="RubberBandCollet2"
  LinkPlacement = pos=(8.5,24.5,4.02331e-07) rot=(0,0.707107,0.707107;3.14159rad)
  LinkedObject = -> <external Assembly_LinkageUnit.FCStd>#RubberBandCollet
  Placement = pos=(8.5,24.5,4.02331e-07) rot=(0,0.707107,0.707107;3.14159rad)
FEATURE [App::Link] RubberBandCollet002  label="RubberBandCollet3"
  LinkPlacement = pos=(-8.5,-24.5,-1.1921e-07) rot=(1,0,0;1.5708rad)
  LinkedObject = -> <external Assembly_LinkageUnit.FCStd>#RubberBandCollet002
  Placement = pos=(-8.5,-24.5,-1.1921e-07) rot=(1,0,0;1.5708rad)
FEATURE [App::Link] RubberBandCollet003  label="RubberBandCollet4"
  LinkPlacement = pos=(8.5,-24.5,9.98377e-07) rot=(-1,0,0;1.5708rad)
  LinkedObject = -> <external Assembly_LinkageUnit.FCStd>#RubberBandCollet003
  Placement = pos=(8.5,-24.5,9.98377e-07) rot=(-1,0,0;1.5708rad)
FEATURE [App::Link] MotorMount
  LinkPlacement = pos=(0,0,-10.5) rot=(0.707107,0.707107,0;3.14159rad)
  LinkedObject = -> <external MotorMount.FCStd>#Body
  Placement = pos=(0,0,-10.5) rot=(0.707107,0.707107,0;3.14159rad)
FEATURE [Part::FeaturePython] Screw  label="M3x10-Screw"  # WARN: FeaturePython — macro-defined, semantics opaque (R4)
  BaseObject = -> MotorMount [Fillet020.Edge284]
  Diameter = 3
  Invert = false
  LeftHanded = false
  Length = 1
  LengthCustom = 10
  MatchOuter = false
  OffsetAngle = 0
  Placement = pos=(15.5,15.5,-10.5) rot=(1.0625,0,0;0rad)
  Thread = false
  Type = 55
FEATURE [Part::FeaturePython] Screw001  label="M3x10-Screw008"  # WARN: FeaturePython — macro-defined, semantics opaque (R4)
  BaseObject = -> MotorMount [Fillet020.Edge282]
  Diameter = 3
  Invert = false
  LeftHanded = false
  Length = 1
  LengthCustom = 10
  MatchOuter = false
  OffsetAngle = 0
  Placement = pos=(-15.5,15.5,-10.5) rot=(1.0625,0,0;0rad)
  Thread = false
  Type = 55
FEATURE [Part::FeaturePython] Screw002  label="M3x10-Screw009"  # WARN: FeaturePython — macro-defined, semantics opaque (R4)
  BaseObject = -> MotorMount [Fillet020.Edge262]
  Diameter = 3
  Invert = false
  LeftHanded = false
  Length = 1
  LengthCustom = 10
  MatchOuter = false
  OffsetAngle = 0
  Placement = pos=(-15.5,-15.5,-10.5) rot=(1.0625,0,0;0rad)
  Thread = false
  Type = 55
FEATURE [Part::FeaturePython] Screw003  label="M3x6-Screw"  # WARN: FeaturePython — macro-defined, semantics opaque (R4)
  BaseObject = -> MotorMount [Fillet020.Edge150]
  Diameter = 3
  Invert = false
  LeftHanded = false
  Length = 8
  LengthCustom = 6
  MatchOuter = false
  Offset = 1
  OffsetAngle = 0
  Placement = pos=(15.5,-15.5,-14.5) rot=(1.0625,0,0;0rad)
  Thread = false
  Type = 55
FEATURE [Part::FeaturePython] Pin  label="2 mmx8-Pin"  # WARN: FeaturePython — macro-defined, semantics opaque (R4)
  BaseObject = -> LinkageUnit [BallJointPlate.Fillet001.;#32c:1;:H36d,E.Edge55]
  Diameter = 3
  Invert = false
  LeftHanded = false
  Length = 2
  LengthCustom = 8
  OffsetAngle = 0
  Placement = pos=(12,0.299999,4.75) rot=(1,0,0;1.5708rad)
  Thread = false
  Type = 9
FEATURE [Part::FeaturePython] Pin001  label="2 mmx8-Pin012"  # WARN: FeaturePython — macro-defined, semantics opaque (R4)
  BaseObject = -> LinkageUnit [BallJointPlate.Fillet001.;#32e:1;:H36d,E.Edge57]
  Diameter = 3
  Invert = true
  LeftHanded = false
  Length = 2
  LengthCustom = 8
  OffsetAngle = 0
  Placement = pos=(12,0.300001,-4.75) rot=(1,0,0;1.5708rad)
  Thread = false
  Type = 9
FEATURE [Part::FeaturePython] Screw004  label="M2x8-Screw"  # WARN: FeaturePython — macro-defined, semantics opaque (R4)
  BaseObject = -> LinkageUnit [BallJointPlate.Fillet001.;#32c:2;:H36d,E.Edge60]
  Diameter = 1
  Invert = false
  LeftHanded = false
  Length = 4
  LengthCustom = 8
  MatchOuter = false
  OffsetAngle = 0
  Placement = pos=(15,0.299999,4.75) rot=(1,0,0;1.5708rad)
  Thread = false
  Type = 57
FEATURE [Part::FeaturePython] Screw005  label="M2x8-Screw009"  # WARN: FeaturePython — macro-defined, semantics opaque (R4)
  BaseObject = -> LinkageUnit [BallJointPlate.Fillet001.;#32e:2;:H36d,E.Edge62]
  Diameter = 1
  Invert = true
  LeftHanded = false
  Length = 4
  LengthCustom = 8
  MatchOuter = false
  OffsetAngle = 0
  Placement = pos=(15,0.300001,-4.75) rot=(1,0,0;1.5708rad)
  Thread = false
  Type = 57
FEATURE [Part::FeaturePython] Screw006  label="M2x8-Screw004"  # WARN: FeaturePython — macro-defined, semantics opaque (R4)
  BaseObject = -> MT6835 [Chamfer001.Edge90]
  Diameter = 1
  Invert = true
  LeftHanded = false
  Length = 4
  LengthCustom = 8
  MatchOuter = false
  OffsetAngle = 0
  Placement = pos=(-34.1,1.41501e-05,-16) rot=(0,-1,0;1.5708rad)
  Thread = false
  Type = 57
FEATURE [Part::FeaturePython] Pin002  label="2 mmx8-Pin011"  # WARN: FeaturePython — macro-defined, semantics opaque (R4)
  BaseObject = -> MotorHorn [Chamfer008.Edge299]
  Diameter = 3
  Invert = false
  LeftHanded = false
  Length = 2
  LengthCustom = 8
  Offset = -0.5
  OffsetAngle = 0
  Placement = pos=(-13,1.54972e-05,-3.75001) rot=(0,0,1;0rad)
  Thread = false
  Type = 9
FEATURE [Part::FeaturePython] Screw007  label="M3x6-Screw003"  # WARN: FeaturePython — macro-defined, semantics opaque (R4)
  BaseObject = -> MotorHorn [Chamfer008.Edge112]
  Diameter = 6
  Invert = true
  LeftHanded = false
  Length = 4
  LengthCustom = 6
  MatchOuter = false
  OffsetAngle = 0
  Placement = pos=(8.34465e-06,7.90002,1.99999) rot=(-1,0,0;1.5708rad)
  Thread = false
  Type = 70
FEATURE [Part::FeaturePython] Screw008  label="M3x6-Screw004"  # WARN: FeaturePython — macro-defined, semantics opaque (R4)
  BaseObject = -> MotorHorn [Chamfer008.Edge116]
  Diameter = 6
  Invert = true
  LeftHanded = false
  Length = 4
  LengthCustom = 6
  MatchOuter = false
  OffsetAngle = 0
  Placement = pos=(8.34465e-06,7.90002,-7.00001) rot=(-1,0,0;1.5708rad)
  Thread = false
  Type = 70
FEATURE [App::DocumentObjectGroup] Group  label="Fasteners"
  Group = -> [Screw,Screw001,Screw002,Screw003,Pin,Pin001,Screw004,Screw005,Screw006,Pin002,Screw007,Screw008]
FEATURE [App::Point] Origin005  label="Origin006"
  Role = Origin
FEATURE [App::Link] BallJointPlate
  LinkPlacement = pos=(0,0,-1.9) rot=(0,0,1;0rad)
  LinkedObject = -> <external Assembly_BallJointPlate.FCStd>#BallJointPlate
  Placement = pos=(0,0,-1.9) rot=(0,0,1;0rad)
FEATURE [App::Link] Ball  label="Ball1"
  LinkPlacement = pos=(8.5,0,0) rot=(0,0,1;0rad)
  LinkedObject = -> <external Assembly_BallJointPlate.FCStd>#Ball
  Placement = pos=(8.5,0,0) rot=(0,0,1;0rad)
FEATURE [App::Link] Ball001  label="Ball2"
  LinkPlacement = pos=(-8.5,0,0) rot=(0,0,1;0rad)
  LinkedObject = -> <external Assembly_BallJointPlate.FCStd>#Ball001
  Placement = pos=(-8.5,0,0) rot=(0,0,1;0rad)
FEATURE [App::Link] RubberBand  label="RubberBand1"
  LinkPlacement = pos=(8.5,0,13.35) rot=(-0.57735,0.57735,0.57735;4.18879rad)
  LinkedObject = -> <external Assembly_BallJointPlate.FCStd>#RubberBand
  Placement = pos=(8.5,0,13.35) rot=(-0.57735,0.57735,0.57735;4.18879rad)
FEATURE [App::Link] RubberBand001  label="RubberBand2"
  LinkPlacement = pos=(-8.5,0,13.35) rot=(0.57735,0.57735,0.57735;2.0944rad)
  LinkedObject = -> <external Assembly_BallJointPlate.FCStd>#RubberBand001
  Placement = pos=(-8.5,0,13.35) rot=(0.57735,0.57735,0.57735;2.0944rad)
FEATURE [App::Link] CrimpBead  label="CrimpBead1a"
  LinkPlacement = pos=(8.5,1.75,-2.4) rot=(0,0,1;1.5708rad)
  LinkedObject = -> <external Assembly_BallJointPlate.FCStd>#CrimpBead
  Placement = pos=(8.5,1.75,-2.4) rot=(0,0,1;1.5708rad)
FEATURE [App::Link] CrimpBead001  label="CrimpBead1b"
  LinkPlacement = pos=(8.5,-1.75,-2.4) rot=(0,0,1;1.5708rad)
  LinkedObject = -> <external Assembly_BallJointPlate.FCStd>#CrimpBead001
  Placement = pos=(8.5,-1.75,-2.4) rot=(0,0,1;1.5708rad)
FEATURE [App::Link] CrimpBead002  label="CrimpBead2a"
  LinkPlacement = pos=(-8.5,1.75,-2.4) rot=(0,0,-1;1.5708rad)
  LinkedObject = -> <external Assembly_BallJointPlate.FCStd>#CrimpBead002
  Placement = pos=(-8.5,1.75,-2.4) rot=(0,0,-1;1.5708rad)
FEATURE [App::Link] CrimpBead003  label="CrimpBead2b"
  LinkPlacement = pos=(-8.5,-1.75,-2.4) rot=(0,0,-1;1.5708rad)
  LinkedObject = -> <external Assembly_BallJointPlate.FCStd>#CrimpBead003
  Placement = pos=(-8.5,-1.75,-2.4) rot=(0,0,-1;1.5708rad)
FEATURE [Assembly::AssemblyLink] BallJointPlateAsm
  Group = -> [BallJointPlate,Ball,Ball001,RubberBand,RubberBand001,CrimpBead,CrimpBead001,CrimpBead002,CrimpBead003]
  LinkedObject = -> <external Assembly_LinkageUnit.FCStd>#BallJointPlateAsm
  Origin = -> Origin004
  Placement = pos=(0,36.25,0) rot=(1,0,0;1.5708rad)
  Rigid = true
FEATURE [App::Point] Origin007  label="Origin009"
  Role = Origin
FEATURE [App::Link] BallJointPlate001
  LinkPlacement = pos=(0,0,-1.9) rot=(0,0,1;0rad)
  LinkedObject = -> <external Assembly_BallJointPlate.FCStd>#BallJointPlate
  Placement = pos=(0,0,-1.9) rot=(0,0,1;0rad)
FEATURE [App::Link] Ball002  label="Ball001"
  LinkPlacement = pos=(8.5,0,0) rot=(0,0,1;0rad)
  LinkedObject = -> <external Assembly_BallJointPlate.FCStd>#Ball
  Placement = pos=(8.5,0,0) rot=(0,0,1;0rad)
FEATURE [App::Link] Ball003  label="Ball002"
  LinkPlacement = pos=(-8.5,0,0) rot=(0,0,1;0rad)
  LinkedObject = -> <external Assembly_BallJointPlate.FCStd>#Ball001
  Placement = pos=(-8.5,0,0) rot=(0,0,1;0rad)
FEATURE [App::Link] RubberBand002  label="RubberBand001"
  LinkPlacement = pos=(8.5,0,13.35) rot=(-0.57735,0.57735,0.57735;4.18879rad)
  LinkedObject = -> <external Assembly_BallJointPlate.FCStd>#RubberBand
  Placement = pos=(8.5,0,13.35) rot=(-0.57735,0.57735,0.57735;4.18879rad)
FEATURE [App::Link] RubberBand003  label="RubberBand002"
  LinkPlacement = pos=(-8.5,0,13.35) rot=(0.57735,0.57735,0.57735;2.0944rad)
  LinkedObject = -> <external Assembly_BallJointPlate.FCStd>#RubberBand001
  Placement = pos=(-8.5,0,13.35) rot=(0.57735,0.57735,0.57735;2.0944rad)
FEATURE [App::Link] CrimpBead004  label="CrimpBead1a001"
  LinkPlacement = pos=(8.5,1.75,-2.4) rot=(0,0,1;1.5708rad)
  LinkedObject = -> <external Assembly_BallJointPlate.FCStd>#CrimpBead
  Placement = pos=(8.5,1.75,-2.4) rot=(0,0,1;1.5708rad)
FEATURE [App::Link] CrimpBead005  label="CrimpBead1b001"
  LinkPlacement = pos=(8.5,-1.75,-2.4) rot=(0,0,1;1.5708rad)
  LinkedObject = -> <external Assembly_BallJointPlate.FCStd>#CrimpBead001
  Placement = pos=(8.5,-1.75,-2.4) rot=(0,0,1;1.5708rad)
FEATURE [App::Link] CrimpBead006  label="CrimpBead2a001"
  LinkPlacement = pos=(-8.5,1.75,-2.4) rot=(0,0,-1;1.5708rad)
  LinkedObject = -> <external Assembly_BallJointPlate.FCStd>#CrimpBead002
  Placement = pos=(-8.5,1.75,-2.4) rot=(0,0,-1;1.5708rad)
FEATURE [App::Link] CrimpBead007  label="CrimpBead2b001"
  LinkPlacement = pos=(-8.5,-1.75,-2.4) rot=(0,0,-1;1.5708rad)
  LinkedObject = -> <external Assembly_BallJointPlate.FCStd>#CrimpBead003
  Placement = pos=(-8.5,-1.75,-2.4) rot=(0,0,-1;1.5708rad)
FEATURE [Assembly::AssemblyLink] BallJointPlateAsm001  label="BallJointPlateAsm"
  Group = -> [BallJointPlate001,Ball002,Ball003,RubberBand002,RubberBand003,CrimpBead004,CrimpBead005,CrimpBead006,CrimpBead007]
  LinkedObject = -> <external Assembly_LinkageUnit.FCStd>#BallJointPlateAsm001
  Origin = -> Origin006
  Placement = pos=(0,-36.25,0) rot=(0,0.707107,0.707107;3.14159rad)
  Rigid = true
FEATURE [Assembly::AssemblyLink] LinkageUnit
  Group = -> [LinkageRod,LinkageRod001,RubberBandCollet001,RubberBandCollet,RubberBandCollet002,RubberBandCollet003,BallJointPlateAsm,BallJointPlateAsm001]
  LinkedObject = -> <external Assembly_LinkageUnit.FCStd>#Assembly
  Origin = -> Origin002
  Placement = pos=(15,-36.25,-9.53674e-07) rot=(0,1,0;1.5708rad)
  Rigid = true
FEATURE [Assembly::AssemblyObject] Assembly  label="Actuator"
  Group = -> [Joints,MotorMount,StepperMotorNema17,MotorHorn,LinkageUnit,EncoderMAgnetArray,MT6835,Screw,Screw001,Screw002,Screw003,Pin,Pin001,Screw004,Screw005,Screw006,Group,Pin002,Screw007,Screw008]
  Origin = -> Origin
  Type = Assembly
---- part Assembly_BallJointPlate.FCStd = doc fcstd_96c2e58f8617 ----
FCSTD DOCUMENT  (FreeCAD 1.2R45225 (Git))
Label: Assembly_BallJointPlate
License: All rights reserved
objects: App::Link×9, App::FeaturePython×9, App::Point×1, Assembly::JointGroup×1, Assembly::AssemblyObject×1
EXTERNAL_REF file=BallJointPlate.FCStd obj=Body
EXTERNAL_REF file=JointBall.FCStd obj=Body
EXTERNAL_REF file=RubberBand.FCStd obj=Body
EXTERNAL_REF file=CrimpBead.FCStd obj=Body

FEATURE [App::Point] Origin001
  Role = Origin
FEATURE [App::Link] BallJointPlate
  LinkPlacement = pos=(0,0,-1.9) rot=(0,0,1;0rad)
  LinkedObject = -> <external BallJointPlate.FCStd>#Body
  Placement = pos=(0,0,-1.9) rot=(0,0,1;0rad)
FEATURE [App::FeaturePython] GroundedJoint  # Assembly grounded joint (typed FeaturePython)
  ObjectToGround = -> BallJointPlate
FEATURE [App::Link] Ball  label="Ball1"
  LinkPlacement = pos=(8.5,0,0) rot=(0,0,1;0rad)
  LinkedObject = -> <external JointBall.FCStd>#Body
  Placement = pos=(8.5,0,0) rot=(0,0,1;0rad)
FEATURE [App::Link] Ball001  label="Ball2"
  LinkPlacement = pos=(-8.5,0,0) rot=(0,0,1;0rad)
  LinkedObject = -> <external JointBall.FCStd>#Body
  Placement = pos=(-8.5,0,0) rot=(0,0,1;0rad)
FEATURE [App::FeaturePython] Joint  label="ball1"  # Assembly joint (typed FeaturePython)
  Angle = 0
  AngleMax = 0
  AngleMin = 0
  Detach1 = false
  Detach2 = false
  Distance = 0
  Distance2 = 0
  EnableAngleMax = false
  EnableAngleMin = false
  EnableLengthMax = false
  EnableLengthMin = false
  JointType = 0 (Fixed)
  LengthMax = 0
  LengthMin = 0
  Offset1 = pos=(8.5,0,1.9) rot=(0,0,1;0rad)
  Placement1 = pos=(8.5,0,1.9) rot=(0,0,1;0rad)
  Reference1 = -> BallJointPlate
  Reference2 = -> Ball
  Suppressed = false
FEATURE [App::FeaturePython] Joint001  label="ball2"  # Assembly joint (typed FeaturePython)
  Angle = 0
  AngleMax = 0
  AngleMin = 0
  Detach1 = false
  Detach2 = false
  Distance = 0
  Distance2 = 0
  EnableAngleMax = false
  EnableAngleMin = false
  EnableLengthMax = false
  EnableLengthMin = false
  JointType = 0 (Fixed)
  LengthMax = 0
  LengthMin = 0
  Offset1 = pos=(-8.5,0,1.9) rot=(0,0,1;0rad)
  Placement1 = pos=(-8.5,0,1.9) rot=(0,0,1;0rad)
  Reference1 = -> BallJointPlate
  Reference2 = -> Ball001
  Suppressed = false
FEATURE [App::Link] RubberBand  label="RubberBand1"
  LinkPlacement = pos=(8.5,0,13.35) rot=(-0.57735,0.57735,0.57735;4.18879rad)
  LinkedObject = -> <external RubberBand.FCStd>#Body
  Placement = pos=(8.5,0,13.35) rot=(-0.57735,0.57735,0.57735;4.18879rad)
FEATURE [App::Link] RubberBand001  label="RubberBand2"
  LinkPlacement = pos=(-8.5,0,13.35) rot=(0.57735,0.57735,0.57735;2.0944rad)
  LinkedObject = -> <external RubberBand.FCStd>#Body
  Placement = pos=(-8.5,0,13.35) rot=(0.57735,0.57735,0.57735;2.0944rad)
FEATURE [App::FeaturePython] Joint002  label="rubber_band1"  # Assembly joint (typed FeaturePython)
  Angle = 0
  AngleMax = 0
  AngleMin = 0
  Detach1 = false
  Detach2 = false
  Distance = 0
  Distance2 = 0
  EnableAngleMax = false
  EnableAngleMin = false
  EnableLengthMax = false
  EnableLengthMin = false
  JointType = 0 (Fixed)
  LengthMax = 0
  LengthMin = 0
  Offset2 = pos=(8.5,0,15.25) rot=(0.57735,-0.57735,-0.57735;2.0944rad)
  Placement2 = pos=(8.5,0,15.25) rot=(0.57735,-0.57735,-0.57735;2.0944rad)
  Reference1 = -> RubberBand
  Reference2 = -> BallJointPlate
  Suppressed = false
FEATURE [App::FeaturePython] Joint003  label="rubber_band2"  # Assembly joint (typed FeaturePython)
  Angle = 0
  AngleMax = 0
  AngleMin = 0
  Detach1 = false
  Detach2 = false
  Distance = 0
  Distance2 = 0
  EnableAngleMax = false
  EnableAngleMin = false
  EnableLengthMax = false
  EnableLengthMin = false
  JointType = 0 (Fixed)
  LengthMax = 0
  LengthMin = 0
  Offset2 = pos=(-8.5,0,15.25) rot=(0.57735,0.57735,0.57735;2.0944rad)
  Placement2 = pos=(-8.5,0,15.25) rot=(0.57735,0.57735,0.57735;2.0944rad)
  Reference1 = -> RubberBand001
  Reference2 = -> BallJointPlate
  Suppressed = false
FEATURE [App::Link] CrimpBead  label="CrimpBead1a"
  LinkPlacement = pos=(8.5,1.75,-2.4) rot=(0,0,1;1.5708rad)
  LinkedObject = -> <external CrimpBead.FCStd>#Body
  Placement = pos=(8.5,1.75,-2.4) rot=(0,0,1;1.5708rad)
FEATURE [App::Link] CrimpBead001  label="CrimpBead1b"
  LinkPlacement = pos=(8.5,-1.75,-2.4) rot=(0,0,1;1.5708rad)
  LinkedObject = -> <external CrimpBead.FCStd>#Body
  Placement = pos=(8.5,-1.75,-2.4) rot=(0,0,1;1.5708rad)
FEATURE [App::FeaturePython] Joint004  label="crimp_bead1a"  # Assembly joint (typed FeaturePython)
  Angle = 0
  AngleMax = 0
  AngleMin = 0
  Detach1 = false
  Detach2 = false
  Distance = 0
  Distance2 = 0
  EnableAngleMax = false
  EnableAngleMin = false
  EnableLengthMax = false
  EnableLengthMin = false
  JointType = 0 (Fixed)
  LengthMax = 0
  LengthMin = 0
  Offset2 = pos=(8.5,1.75,-0.5) rot=(0,0,1;1.5708rad)
  Placement2 = pos=(8.5,1.75,-0.5) rot=(0,0,1;1.5708rad)
  Reference1 = -> CrimpBead
  Reference2 = -> BallJointPlate
  Suppressed = false
FEATURE [App::FeaturePython] Joint005  label="crimp_bead1b"  # Assembly joint (typed FeaturePython)
  Angle = 0
  AngleMax = 0
  AngleMin = 0
  Detach1 = false
  Detach2 = false
  Distance = 0
  Distance2 = 0
  EnableAngleMax = false
  EnableAngleMin = false
  EnableLengthMax = false
  EnableLengthMin = false
  JointType = 0 (Fixed)
  LengthMax = 0
  LengthMin = 0
  Offset2 = pos=(8.5,-1.75,-0.5) rot=(0,0,1;1.5708rad)
  Placement2 = pos=(8.5,-1.75,-0.5) rot=(0,0,1;1.5708rad)
  Reference1 = -> CrimpBead001
  Reference2 = -> BallJointPlate
  Suppressed = false
FEATURE [App::Link] CrimpBead002  label="CrimpBead2a"
  LinkPlacement = pos=(-8.5,1.75,-2.4) rot=(0,0,-1;1.5708rad)
  LinkedObject = -> <external CrimpBead.FCStd>#Body
  Placement = pos=(-8.5,1.75,-2.4) rot=(0,0,-1;1.5708rad)
FEATURE [App::Link] CrimpBead003  label="CrimpBead2b"
  LinkPlacement = pos=(-8.5,-1.75,-2.4) rot=(0,0,-1;1.5708rad)
  LinkedObject = -> <external CrimpBead.FCStd>#Body
  Placement = pos=(-8.5,-1.75,-2.4) rot=(0,0,-1;1.5708rad)
FEATURE [App::FeaturePython] Joint006  label="crimp_bead2b"  # Assembly joint (typed FeaturePython)
  Angle = 0
  AngleMax = 0
  AngleMin = 0
  Detach1 = false
  Detach2 = false
  Distance = 0
  Distance2 = 0
  EnableAngleMax = false
  EnableAngleMin = false
  EnableLengthMax = false
  EnableLengthMin = false
  JointType = 0 (Fixed)
  LengthMax = 0
  LengthMin = 0
  Offset2 = pos=(-8.5,-1.75,-0.5) rot=(0,0,-1;1.5708rad)
  Placement2 = pos=(-8.5,-1.75,-0.5) rot=(0,0,-1;1.5708rad)
  Reference1 = -> CrimpBead003
  Reference2 = -> BallJointPlate
  Suppressed = false
FEATURE [App::FeaturePython] Joint007  label="Fixed009"  # Assembly joint (typed FeaturePython)
  Angle = 0
  AngleMax = 0
  AngleMin = 0
  Detach1 = false
  Detach2 = false
  Distance = 0
  Distance2 = 0
  EnableAngleMax = false
  EnableAngleMin = false
  EnableLengthMax = false
  EnableLengthMin = false
  JointType = 0 (Fixed)
  LengthMax = 0
  LengthMin = 0
  Offset2 = pos=(-8.5,1.75,-0.5) rot=(0,0,-1;1.5708rad)
  Placement2 = pos=(-8.5,1.75,-0.5) rot=(0,0,-1;1.5708rad)
  Reference1 = -> CrimpBead002
  Reference2 = -> BallJointPlate
  Suppressed = false
FEATURE [Assembly::JointGroup] Joints
  Group = -> [GroundedJoint,Joint,Joint001,Joint002,Joint003,Joint004,Joint005,Joint006,Joint007]
FEATURE [Assembly::AssemblyObject] Assembly  label="BallJointPlateAsm"
  Group = -> [Joints,BallJointPlate,GroundedJoint,Ball,Ball001,Joint,Joint001,RubberBand,RubberBand001,Joint002,Joint003,CrimpBead,CrimpBead001,Joint004,Joint005,CrimpBead002,CrimpBead003,Joint006,Joint007]
  Origin = -> Origin
  Type = Assembly
---- part Assembly_LinkageUnit.FCStd = doc fcstd_ba4d1da7e42f ----
FCSTD DOCUMENT  (FreeCAD 1.2R45225 (Git))
Label: Assembly_LinkageUnit
License: All rights reserved
LicenseURL: https://en.wikipedia.org/wiki/All_rights_reserved
objects: App::Link×24, App::FeaturePython×8, App::Point×3, Assembly::AssemblyLink×2, Assembly::JointGroup×1, Assembly::AssemblyObject×1
EXTERNAL_REF file=RubberBandCollet.FCStd obj=Body
EXTERNAL_REF file=LinkageRod.FCStd obj=Body
EXTERNAL_REF file=Assembly_BallJointPlate.FCStd obj=Assembly
EXTERNAL_REF file=Assembly_BallJointPlate.FCStd obj=BallJointPlate
EXTERNAL_REF file=Assembly_BallJointPlate.FCStd obj=Ball
EXTERNAL_REF file=Assembly_BallJointPlate.FCStd obj=Ball001
EXTERNAL_REF file=Assembly_BallJointPlate.FCStd obj=RubberBand
EXTERNAL_REF file=Assembly_BallJointPlate.FCStd obj=RubberBand001
EXTERNAL_REF file=Assembly_BallJointPlate.FCStd obj=CrimpBead
EXTERNAL_REF file=Assembly_BallJointPlate.FCStd obj=CrimpBead001
EXTERNAL_REF file=Assembly_BallJointPlate.FCStd obj=CrimpBead002
EXTERNAL_REF file=Assembly_BallJointPlate.FCStd obj=CrimpBead003

FEATURE [App::Point] Origin001
  Role = Origin
FEATURE [App::Link] RubberBandCollet  label="RubberBandCollet2"
  LinkPlacement = pos=(8.5,24.5,4.02331e-07) rot=(0,0.707107,0.707107;3.14159rad)
  LinkedObject = -> <external RubberBandCollet.FCStd>#Body
  Placement = pos=(8.5,24.5,4.02331e-07) rot=(0,0.707107,0.707107;3.14159rad)
FEATURE [App::Link] RubberBandCollet001  label="RubberBandCollet1"
  LinkPlacement = pos=(-8.5,24.5,5.51344e-07) rot=(0,0.707107,0.707107;3.14159rad)
  LinkedObject = -> <external RubberBandCollet.FCStd>#Body
  Placement = pos=(-8.5,24.5,5.51344e-07) rot=(0,0.707107,0.707107;3.14159rad)
FEATURE [App::Link] RubberBandCollet002  label="RubberBandCollet3"
  LinkPlacement = pos=(-8.5,-24.5,-1.1921e-07) rot=(1,0,0;1.5708rad)
  LinkedObject = -> <external RubberBandCollet.FCStd>#Body
  Placement = pos=(-8.5,-24.5,-1.1921e-07) rot=(1,0,0;1.5708rad)
FEATURE [App::Link] RubberBandCollet003  label="RubberBandCollet4"
  LinkPlacement = pos=(8.5,-24.5,9.98377e-07) rot=(-1,0,0;1.5708rad)
  LinkedObject = -> <external RubberBandCollet.FCStd>#Body
  Placement = pos=(8.5,-24.5,9.98377e-07) rot=(-1,0,0;1.5708rad)
FEATURE [App::Link] LinkageRod  label="LinkageRod1"
  LinkPlacement = pos=(8.5,0,0) rot=(0,0,1;0rad)
  LinkedObject = -> <external LinkageRod.FCStd>#Body
  Placement = pos=(8.5,0,0) rot=(0,0,1;0rad)
FEATURE [App::Link] LinkageRod001  label="LinkageRod2"
  LinkPlacement = pos=(-8.5,0,0) rot=(0,0,1;0rad)
  LinkedObject = -> <external LinkageRod.FCStd>#Body
  Placement = pos=(-8.5,0,0) rot=(0,0,1;0rad)
FEATURE [App::Point] Origin003
  Role = Origin
FEATURE [App::Link] BallJointPlate002  label="BallJointPlate"
  LinkPlacement = pos=(0,0,-1.9) rot=(0,0,1;0rad)
  LinkedObject = -> <external Assembly_BallJointPlate.FCStd>#BallJointPlate
  Placement = pos=(0,0,-1.9) rot=(0,0,1;0rad)
FEATURE [App::Link] Ball004  label="Ball001"
  LinkPlacement = pos=(8.5,0,0) rot=(0,0,1;0rad)
  LinkedObject = -> <external Assembly_BallJointPlate.FCStd>#Ball
  Placement = pos=(8.5,0,0) rot=(0,0,1;0rad)
FEATURE [App::Link] Ball005  label="Ball002"
  LinkPlacement = pos=(-8.5,0,0) rot=(0,0,1;0rad)
  LinkedObject = -> <external Assembly_BallJointPlate.FCStd>#Ball001
  Placement = pos=(-8.5,0,0) rot=(0,0,1;0rad)
FEATURE [App::Link] RubberBand004  label="RubberBand001"
  LinkPlacement = pos=(8.5,0,13.35) rot=(-0.57735,0.57735,0.57735;4.18879rad)
  LinkedObject = -> <external Assembly_BallJointPlate.FCStd>#RubberBand
  Placement = pos=(8.5,0,13.35) rot=(-0.57735,0.57735,0.57735;4.18879rad)
FEATURE [App::Link] RubberBand005  label="RubberBand002"
  LinkPlacement = pos=(-8.5,0,13.35) rot=(0.57735,0.57735,0.57735;2.0944rad)
  LinkedObject = -> <external Assembly_BallJointPlate.FCStd>#RubberBand001
  Placement = pos=(-8.5,0,13.35) rot=(0.57735,0.57735,0.57735;2.0944rad)
FEATURE [App::Link] CrimpBead  label="CrimpBead1a"
  LinkPlacement = pos=(8.5,1.75,-2.4) rot=(0,0,1;1.5708rad)
  LinkedObject = -> <external Assembly_BallJointPlate.FCStd>#CrimpBead
  Placement = pos=(8.5,1.75,-2.4) rot=(0,0,1;1.5708rad)
FEATURE [App::Link] CrimpBead001  label="CrimpBead1b"
  LinkPlacement = pos=(8.5,-1.75,-2.4) rot=(0,0,1;1.5708rad)
  LinkedObject = -> <external Assembly_BallJointPlate.FCStd>#CrimpBead001
  Placement = pos=(8.5,-1.75,-2.4) rot=(0,0,1;1.5708rad)
FEATURE [App::Link] CrimpBead002  label="CrimpBead2a"
  LinkPlacement = pos=(-8.5,1.75,-2.4) rot=(0,0,-1;1.5708rad)
  LinkedObject = -> <external Assembly_BallJointPlate.FCStd>#CrimpBead002
  Placement = pos=(-8.5,1.75,-2.4) rot=(0,0,-1;1.5708rad)
FEATURE [App::Link] CrimpBead003  label="CrimpBead2b"
  LinkPlacement = pos=(-8.5,-1.75,-2.4) rot=(0,0,-1;1.5708rad)
  LinkedObject = -> <external Assembly_BallJointPlate.FCStd>#CrimpBead003
  Placement = pos=(-8.5,-1.75,-2.4) rot=(0,0,-1;1.5708rad)
FEATURE [Assembly::AssemblyLink] BallJointPlateAsm
  Group = -> [BallJointPlate002,Ball004,Ball005,RubberBand004,RubberBand005,CrimpBead,CrimpBead001,CrimpBead002,CrimpBead003]
  LinkedObject = -> <external Assembly_BallJointPlate.FCStd>#Assembly
  Origin = -> Origin002
  Placement = pos=(0,36.25,0) rot=(1,0,0;1.5708rad)
  Rigid = true
FEATURE [App::Point] Origin005  label="Origin006"
  Role = Origin
FEATURE [App::Link] BallJointPlate003  label="BallJointPlate001"
  LinkPlacement = pos=(0,0,-1.9) rot=(0,0,1;0rad)
  LinkedObject = -> <external Assembly_BallJointPlate.FCStd>#BallJointPlate
  Placement = pos=(0,0,-1.9) rot=(0,0,1;0rad)
FEATURE [App::Link] Ball006  label="Ball003"
  LinkPlacement = pos=(8.5,0,0) rot=(0,0,1;0rad)
  LinkedObject = -> <external Assembly_BallJointPlate.FCStd>#Ball
  Placement = pos=(8.5,0,0) rot=(0,0,1;0rad)
FEATURE [App::Link] Ball007  label="Ball004"
  LinkPlacement = pos=(-8.5,0,0) rot=(0,0,1;0rad)
  LinkedObject = -> <external Assembly_BallJointPlate.FCStd>#Ball001
  Placement = pos=(-8.5,0,0) rot=(0,0,1;0rad)
FEATURE [App::Link] RubberBand006  label="RubberBand003"
  LinkPlacement = pos=(8.5,0,13.35) rot=(-0.57735,0.57735,0.57735;4.18879rad)
  LinkedObject = -> <external Assembly_BallJointPlate.FCStd>#RubberBand
  Placement = pos=(8.5,0,13.35) rot=(-0.57735,0.57735,0.57735;4.18879rad)
FEATURE [App::Link] RubberBand007  label="RubberBand004"
  LinkPlacement = pos=(-8.5,0,13.35) rot=(0.57735,0.57735,0.57735;2.0944rad)
  LinkedObject = -> <external Assembly_BallJointPlate.FCStd>#RubberBand001
  Placement = pos=(-8.5,0,13.35) rot=(0.57735,0.57735,0.57735;2.0944rad)
FEATURE [App::Link] CrimpBead004  label="CrimpBead1a001"
  LinkPlacement = pos=(8.5,1.75,-2.4) rot=(0,0,1;1.5708rad)
  LinkedObject = -> <external Assembly_BallJointPlate.FCStd>#CrimpBead
  Placement = pos=(8.5,1.75,-2.4) rot=(0,0,1;1.5708rad)
FEATURE [App::Link] CrimpBead005  label="CrimpBead1b001"
  LinkPlacement = pos=(8.5,-1.75,-2.4) rot=(0,0,1;1.5708rad)
  LinkedObject = -> <external Assembly_BallJointPlate.FCStd>#CrimpBead001
  Placement = pos=(8.5,-1.75,-2.4) rot=(0,0,1;1.5708rad)
FEATURE [App::Link] CrimpBead006  label="CrimpBead2a001"
  LinkPlacement = pos=(-8.5,1.75,-2.4) rot=(0,0,-1;1.5708rad)
  LinkedObject = -> <external Assembly_BallJointPlate.FCStd>#CrimpBead002
  Placement = pos=(-8.5,1.75,-2.4) rot=(0,0,-1;1.5708rad)
FEATURE [App::Link] CrimpBead007  label="CrimpBead2b001"
  LinkPlacement = pos=(-8.5,-1.75,-2.4) rot=(0,0,-1;1.5708rad)
  LinkedObject = -> <external Assembly_BallJointPlate.FCStd>#CrimpBead003
  Placement = pos=(-8.5,-1.75,-2.4) rot=(0,0,-1;1.5708rad)
FEATURE [Assembly::AssemblyLink] BallJointPlateAsm001  label="BallJointPlateAsm"
  Group = -> [BallJointPlate003,Ball006,Ball007,RubberBand006,RubberBand007,CrimpBead004,CrimpBead005,CrimpBead006,CrimpBead007]
  LinkedObject = -> <external Assembly_BallJointPlate.FCStd>#Assembly
  Origin = -> Origin004
  Placement = pos=(0,-36.25,0) rot=(0,0.707107,0.707107;3.14159rad)
  Rigid = true
FEATURE [App::FeaturePython] GroundedJoint  label="GroundedJoint001"  # Assembly grounded joint (typed FeaturePython)
  ObjectToGround = -> BallJointPlateAsm
FEATURE [App::FeaturePython] GroundedJoint001  label="GroundedJoint002"  # Assembly grounded joint (typed FeaturePython)
  ObjectToGround = -> BallJointPlateAsm001
FEATURE [App::FeaturePython] GroundedJoint002  label="GroundedJoint003"  # Assembly grounded joint (typed FeaturePython)
  ObjectToGround = -> RubberBandCollet003
FEATURE [App::FeaturePython] GroundedJoint003  label="GroundedJoint004"  # Assembly grounded joint (typed FeaturePython)
  ObjectToGround = -> LinkageRod
FEATURE [App::FeaturePython] GroundedJoint004  label="GroundedJoint005"  # Assembly grounded joint (typed FeaturePython)
  ObjectToGround = -> LinkageRod001
FEATURE [App::FeaturePython] GroundedJoint005  label="GroundedJoint006"  # Assembly grounded joint (typed FeaturePython)
  ObjectToGround = -> RubberBandCollet001
FEATURE [App::FeaturePython] GroundedJoint006  label="GroundedJoint007"  # Assembly grounded joint (typed FeaturePython)
  ObjectToGround = -> RubberBandCollet
FEATURE [App::FeaturePython] GroundedJoint007  label="GroundedJoint008"  # Assembly grounded joint (typed FeaturePython)
  ObjectToGround = -> RubberBandCollet002
FEATURE [Assembly::JointGroup] Joints
  Group = -> [GroundedJoint,GroundedJoint001,GroundedJoint002,GroundedJoint003,GroundedJoint004,GroundedJoint005,GroundedJoint006,GroundedJoint007]
FEATURE [Assembly::AssemblyObject] Assembly  label="LinkageUnit"
  Group = -> [Joints,LinkageRod,LinkageRod001,RubberBandCollet001,RubberBandCollet,RubberBandCollet002,RubberBandCollet003,BallJointPlateAsm,BallJointPlateAsm001,GroundedJoint,GroundedJoint001,GroundedJoint002,GroundedJoint003,GroundedJoint004,GroundedJoint005,GroundedJoint006,GroundedJoint007]
  Origin = -> Origin
  Type = Assembly
---- part BaseBlock.FCStd = doc fcstd_f7c52f9150f9 ----
FCSTD DOCUMENT  (FreeCAD 1.2R45145 (Git))
Label: BaseBlock
License: All rights reserved
LicenseURL: https://en.wikipedia.org/wiki/All_rights_reserved
objects: Sketcher::SketchObject×4, PartDesign::Pocket×3, PartDesign::Chamfer×2, PartDesign::Fillet×2, App::Point×1, PartDesign::Pad×1, Part::DatumLine×1, PartDesign::PolarPattern×1, Part::DatumPlane×1, PartDesign::Body×1
note: 35 computed .brp shape members not serialized (recipe doc carries the construction recipe); baked Part::Feature solids carry a one-line shape summary decoded from their .brp

FEATURE [App::Point] Origin001
  Role = Origin
FEATURE [Sketcher::SketchObject] Sketch
  ArcFitTolerance = 1e-06
  AttachmentSupport = -> [Origin]
  ExternalTypes = [0]
  FullyConstrained = true
  MakeInternals = false
  MapMode = 5
  sketch-geometry (5):
    g0: LineSegment StartX=0 StartY=0 StartZ=0 EndX=34.5 EndY=0 EndZ=0
    g1: LineSegment StartX=34.5 StartY=0 StartZ=0 EndX=34.5 EndY=34.5 EndZ=0
    g2: LineSegment StartX=34.5 StartY=34.5 StartZ=0 EndX=0 EndY=34.5 EndZ=0
    g3: LineSegment StartX=0 StartY=34.5 StartZ=0 EndX=0 EndY=0 EndZ=0
    g4: GeomPoint [constr] X=0 Y=0 Z=0
  constraints (12):
    c: Coincident(g0,g1)
    c: Coincident(g1,g2)
    c: Coincident(g2,g3)
    c: Coincident(g3,g0)
    c: Horizontal(g0)
    c: Horizontal(g2)
    c: Vertical(g1)
    c: Vertical(g3)
    c: Coincident(g4,g-1)
    c: DistanceY(g1,g1) = 34.5
    c: DistanceX(g0,g0) = 34.5
    c: Coincident(g0,g4)
FEATURE [PartDesign::Pad] Pad
  Direction = (0,0,1)
  Length = 34.5
  Length2 = 10
  Profile = -> Sketch
  ReferenceAxis = -> Sketch [N_Axis]
  Refine = true
  SideType = 0
  Suppressed = false
  Type = 0
  Type2 = 0
FEATURE [Part::DatumLine] DatumLine
  AttacherType = Attacher::AttachEngineLine
  AttachmentSupport = -> [Pad]
  MapMode = 29
  Placement = pos=(7.1e-15,7.1e-15,7.1e-15) rot=(0.90627,-0.375389,-0.194316;2.26431rad)
FEATURE [Sketcher::SketchObject] Sketch001
  ArcFitTolerance = 1e-06
  AttachmentSupport = -> [Pad]
  ExternalTypes = [0]
  FullyConstrained = false
  MakeInternals = false
  MapMode = 5
  Placement = pos=(0,0,34.5) rot=(0,0,1;0rad)
  sketch-geometry (9):
    g0: LineSegment StartX=0 StartY=0 StartZ=0 EndX=25 EndY=0 EndZ=0
    g1: LineSegment StartX=25 StartY=0 StartZ=0 EndX=25 EndY=25 EndZ=0
    g2: LineSegment StartX=25 StartY=25 StartZ=0 EndX=0 EndY=25 EndZ=0
    g3: LineSegment StartX=0 StartY=25 StartZ=0 EndX=0 EndY=0 EndZ=0
    g4: LineSegment StartX=-50.6172 StartY=-45.3495 StartZ=0 EndX=50.6172 EndY=-45.3495 EndZ=0
    g5: LineSegment StartX=50.6172 StartY=-45.3495 StartZ=0 EndX=50.6172 EndY=45.3495 EndZ=0
    g6: LineSegment StartX=50.6172 StartY=45.3495 StartZ=0 EndX=-50.6172 EndY=45.3495 EndZ=0
    g7: LineSegment StartX=-50.6172 StartY=45.3495 StartZ=0 EndX=-50.6172 EndY=-45.3495 EndZ=0
    g8: GeomPoint [constr] X=0 Y=0 Z=0
  constraints (21):
    c: Coincident(g0,g1)
    c: Coincident(g1,g2)
    c: Coincident(g2,g3)
    c: Coincident(g3,g0)
    c: Horizontal(g0)
    c: Vertical(g1)
    c: Vertical(g3)
    c: Coincident(g0,g-1)
    c: DistanceX(g0,g0) = 25
    c: DistanceY(g3,g3) = 25
    c: Coincident(g4,g5)
    c: Coincident(g5,g6)
    c: Coincident(g6,g7)
    c: Coincident(g7,g4)
    c: Horizontal(g4)
    c: Horizontal(g6)
    c: Vertical(g5)
    c: Vertical(g7)
    c: Symmetric(g6,g4,g8)
    c: Coincident(g8,g0)
    c: Horizontal(g2)
FEATURE [PartDesign::Pocket] Pocket
  BaseFeature = -> Pad
  Direction = (0,0,-1)
  Length = 9.5
  Length2 = 5
  Profile = -> Sketch001
  ReferenceAxis = -> Sketch001 [N_Axis]
  Refine = true
  SideType = 0
  Suppressed = false
  Type = 0
  Type2 = 0
FEATURE [PartDesign::Chamfer] Chamfer002
  Angle = 80
  Base = -> Pocket [Edge15]
  BaseFeature = -> Pocket
  ChamferType = 2
  FlipDirection = false
  Refine = true
  Size = 3.75
  Size2 = 1
  SupportTransform = false
  Suppressed = false
  UseAllEdges = false
FEATURE [PartDesign::Fillet] Fillet003
  Base = -> Chamfer002 [Edge9]
  BaseFeature = -> Chamfer002
  Radius = 3
  Refine = true
  SupportTransform = false
  Suppressed = false
  UseAllEdges = false
FEATURE [Sketcher::SketchObject] Sketch003
  ArcFitTolerance = 1e-06
  AttachmentSupport = -> [Fillet003]
  ExternalTypes = [0]
  FullyConstrained = true
  MakeInternals = false
  MapMode = 5
  Placement = pos=(0,0,34.5) rot=(0,0,1;0rad)
  sketch-geometry (12):
    g0: LineSegment [constr] StartX=4 StartY=21 StartZ=0 EndX=4 EndY=4 EndZ=0
    g1: LineSegment [constr] StartX=4 StartY=4 StartZ=0 EndX=21 EndY=4 EndZ=0
    g2: LineSegment [constr] StartX=21 StartY=4 StartZ=0 EndX=21 EndY=21 EndZ=0
    g3: LineSegment [constr] StartX=21 StartY=21 StartZ=0 EndX=4 EndY=21 EndZ=0
    g4: GeomPoint [constr] X=12.5 Y=12.5 Z=0
    g5: Circle CenterX=4 CenterY=21 CenterZ=0 NormalX=0 NormalY=0 NormalZ=1 AngleXU=0 Radius=1.35
    g6: Circle CenterX=21 CenterY=18 CenterZ=0 NormalX=0 NormalY=0 NormalZ=1 AngleXU=0 Radius=1.35
    g7: Circle CenterX=21 CenterY=4 CenterZ=0 NormalX=0 NormalY=0 NormalZ=1 AngleXU=0 Radius=1.35
    g8: Circle CenterX=4 CenterY=4 CenterZ=0 NormalX=0 NormalY=0 NormalZ=1 AngleXU=0 Radius=1.35
    g9: Circle CenterX=4 CenterY=12.5 CenterZ=0 NormalX=0 NormalY=0 NormalZ=1 AngleXU=0 Radius=1
    g10: Circle CenterX=21 CenterY=12.5 CenterZ=0 NormalX=0 NormalY=0 NormalZ=1 AngleXU=0 Radius=1
    g11: Circle CenterX=15.5 CenterY=12.5 CenterZ=0 NormalX=0 NormalY=0 NormalZ=1 AngleXU=0 Radius=1.5
  constraints (29):
    c: Coincident(g0,g1)
    c: Coincident(g1,g2)
    c: Coincident(g2,g3)
    c: Coincident(g3,g0)
    c: Vertical(g0)
    c: Vertical(g2)
    c: Horizontal(g1)
    c: Horizontal(g3)
    c: Symmetric(g2,g0,g4)
    c: DistanceY(g2,g2) = 17
    c: Equal(g3,g2)
    c: DistanceX(g-1,g4) = 12.5
    c: DistanceY(g-1,g4) = 12.5
    c: Coincident(g5,g0)
    c: Coincident(g7,g1)
    c: Coincident(g8,g0)
    c: Equal(g8,g5)
    c: Equal(g5,g6)
    c: Equal(g6,g7)
    c: Diameter(g6) = 2.7
    c: Symmetric(g0,g0,g9)
    c: Symmetric(g2,g2,g10)
    c: Equal(g10,g9)
    c: Diameter(g10) = 2
    c: PointOnObject(g6,g2)
    c: DistanceY(g6,g2) = 3
    c: Diameter(g11) = 3
    c: Horizontal(g11,g10)
    c: Distance(g11,g2) = 5.5
FEATURE [PartDesign::Pocket] Pocket002
  BaseFeature = -> Fillet003
  Direction = (0,0,-1)
  Length = 12
  Length2 = 5
  Profile = -> Sketch003
  ReferenceAxis = -> Sketch003 [N_Axis]
  Refine = true
  SideType = 0
  Suppressed = false
  Type = 0
  Type2 = 0
FEATURE [PartDesign::Fillet] Fillet
  Base = -> Pocket002 [Edge11,Edge23]
  BaseFeature = -> Pocket002
  Radius = 1
  Refine = true
  SupportTransform = false
  Suppressed = false
  UseAllEdges = false
FEATURE [PartDesign::PolarPattern] PolarPattern
  Angle = 360
  Axis = -> DatumLine
  BaseFeature = -> Fillet
  Mode = 0
  Occurrences = 3
  Offset = 120
  Originals = -> [Pocket,Chamfer002,Fillet003,Fillet,Pocket002]
  Refine = true
  SpacingPattern = [0]
  Spacings = [-1,-1]
  Suppressed = false
  TransformMode = 0
FEATURE [PartDesign::Chamfer] Chamfer
  Angle = 45
  Base = -> PolarPattern [Edge138,Edge136,Edge137]
  BaseFeature = -> PolarPattern
  ChamferType = 0
  FlipDirection = false
  Refine = true
  Size = 1
  Size2 = 1
  SupportTransform = false
  Suppressed = false
  UseAllEdges = false
FEATURE [Part::DatumPlane] DatumPlane
  AttachmentOffset = pos=(0,0,-44) rot=(-1,0,0;0.017453rad)
  AttachmentSupport = -> [Chamfer]
  MapMode = 5
  Placement = pos=(26.0701,26.0701,26.0701) rot=(0.945239,-0.122263,-0.302612;2.37846rad)
FEATURE [Sketcher::SketchObject] Sketch004
  ArcFitTolerance = 1e-06
  AttachmentSupport = -> [DatumPlane]
  ExternalTypes = [0]
  FullyConstrained = true
  MakeInternals = false
  MapMode = 5
  Placement = pos=(26.0701,26.0701,26.0701) rot=(0.945239,-0.122263,-0.302612;2.37846rad)
  sketch-geometry (1):
    g0: Circle CenterX=0 CenterY=0 CenterZ=0 NormalX=0 NormalY=0 NormalZ=1 AngleXU=0 Radius=4
  constraints (2):
    c: Coincident(g0,g-1)
    c: Diameter(g0) = 8
FEATURE [PartDesign::Pocket] Pocket003
  BaseFeature = -> Chamfer
  Direction = (0.577262,0.589603,0.564922)
  Length = 3.5
  Length2 = 5
  Profile = -> Sketch004
  ReferenceAxis = -> Sketch004 [N_Axis]
  Refine = true
  Reversed = true
  SideType = 0
  Suppressed = false
  Type = 0
  Type2 = 0
FEATURE [PartDesign::Body] Body  label="BaseBlock"
  AllowCompound = false
  Group = -> [Sketch,Pad,DatumLine,Sketch001,Pocket,Chamfer002,Fillet003,Sketch003,Pocket002,Fillet,PolarPattern,Chamfer,DatumPlane,Sketch004,Pocket003]
  Origin = -> Origin
  Tip = -> Pocket003
---- part EndEffector.FCStd = doc fcstd_84fef26d72db ----
FCSTD DOCUMENT  (FreeCAD 1.2R45225 (Git))
Label: EndEffector
License: All rights reserved
LicenseURL: https://en.wikipedia.org/wiki/All_rights_reserved
objects: Sketcher::SketchObject×5, PartDesign::Pocket×4, PartDesign::Fillet×3, Part::DatumPoint×3, Measure::MeasurePosition×3, PartDesign::PolarPattern×2, PartDesign::Chamfer×2, App::Point×1, PartDesign::Pad×1, Part::DatumLine×1, PartDesign::Body×1, App::DocumentObjectGroup×1
note: 45 computed .brp shape members not serialized (recipe doc carries the construction recipe); baked Part::Feature solids carry a one-line shape summary decoded from their .brp

FEATURE [App::Point] Origin001
  Role = Origin
FEATURE [Sketcher::SketchObject] Sketch
  ArcFitTolerance = 1e-06
  AttachmentSupport = -> [XY_Plane]
  ExternalTypes = [0]
  FullyConstrained = true
  MakeInternals = false
  MapMode = 5
  sketch-geometry (5):
    g0: LineSegment StartX=-14.5 StartY=14.5 StartZ=0 EndX=-14.5 EndY=-14.5 EndZ=0
    g1: LineSegment StartX=-14.5 StartY=-14.5 StartZ=0 EndX=14.5 EndY=-14.5 EndZ=0
    g2: LineSegment StartX=14.5 StartY=-14.5 StartZ=0 EndX=14.5 EndY=14.5 EndZ=0
    g3: LineSegment StartX=14.5 StartY=14.5 StartZ=0 EndX=-14.5 EndY=14.5 EndZ=0
    g4: GeomPoint [constr] X=0 Y=0 Z=0
  constraints (12):
    c: Coincident(g0,g1)
    c: Coincident(g1,g2)
    c: Coincident(g2,g3)
    c: Coincident(g3,g0)
    c: Vertical(g0)
    c: Vertical(g2)
    c: Horizontal(g1)
    c: Horizontal(g3)
    c: Symmetric(g2,g0,g4)
    c: Coincident(g4,g-1)
    c: DistanceY(g2,g2) = 29
    c: DistanceX(g1,g1) = 29
FEATURE [PartDesign::Pad] Pad
  Direction = (0,0,1)
  Length = 29
  Length2 = 10
  Profile = -> Sketch
  ReferenceAxis = -> Sketch [N_Axis]
  Refine = true
  SideType = 2
  Suppressed = false
  Type = 0
  Type2 = 0
FEATURE [Part::DatumLine] DatumLine
  AttacherType = Attacher::AttachEngineLine
  AttachmentSupport = -> [Pad]
  MapMode = 29
  Placement = pos=(3.6e-15,3.6e-15,3.6e-15) rot=(0.187053,0.451587,0.872399;2.44807rad)
FEATURE [Sketcher::SketchObject] Sketch002
  ArcFitTolerance = 1e-06
  AttachmentSupport = -> [Pad]
  ExternalTypes = [0,0]
  FullyConstrained = true
  MakeInternals = false
  MapMode = 5
  Placement = pos=(0,-14.5,0) rot=(1,0,0;1.5708rad)
  sketch-geometry (5):
    g0: LineSegment StartX=-24.5 StartY=25 StartZ=0 EndX=-24.5 EndY=-25 EndZ=0
    g1: LineSegment StartX=-24.5 StartY=-25 StartZ=0 EndX=5.5 EndY=-25 EndZ=0
    g2: LineSegment StartX=5.5 StartY=-25 StartZ=0 EndX=5.5 EndY=25 EndZ=0
    g3: LineSegment StartX=5.5 StartY=25 StartZ=0 EndX=-24.5 EndY=25 EndZ=0
    g4: GeomPoint [constr] X=-9.5 Y=0 Z=0
  constraints (13):
    c: Coincident(g0,g1)
    c: Coincident(g1,g2)
    c: Coincident(g2,g3)
    c: Coincident(g3,g0)
    c: Vertical(g0)
    c: Vertical(g2)
    c: Horizontal(g1)
    c: Horizontal(g3)
    c: Symmetric(g2,g0,g4)
    c: PointOnObject(g4,g-1)
    c: DistanceX(g3,g3) = 30
    c: DistanceY(g0,g0) = 50
    c: Distance(g2,g-2) = 5.5
FEATURE [PartDesign::Pocket] Pocket001
  BaseFeature = -> Pad
  Direction = (0,1,0)
  Length = 11.5
  Length2 = 5
  Profile = -> Sketch002
  ReferenceAxis = -> Sketch002 [N_Axis]
  Refine = true
  SideType = 0
  Suppressed = false
  Type = 0
  Type2 = 0
FEATURE [Sketcher::SketchObject] Sketch004
  ArcFitTolerance = 1e-06
  AttachmentSupport = -> [Pocket001]
  ExternalGeometry = -> [Pocket001]
  ExternalTypes = [0,0]
  FullyConstrained = true
  MakeInternals = false
  MapMode = 5
  Placement = pos=(5.5,0,0) rot=(0.57735,-0.57735,-0.57735;2.0944rad)
  sketch-geometry (4):
    g0: LineSegment StartX=14.5 StartY=14.5 StartZ=0 EndX=3 EndY=14.5 EndZ=0
    g1: LineSegment StartX=3 StartY=14.5 StartZ=0 EndX=3 EndY=12 EndZ=0
    g2: LineSegment StartX=3 StartY=12 StartZ=0 EndX=14.5 EndY=12 EndZ=0
    g3: LineSegment StartX=14.5 StartY=12 StartZ=0 EndX=14.5 EndY=14.5 EndZ=0
  constraints (11):
    c: Coincident(g0,g1)
    c: Coincident(g1,g2)
    c: Coincident(g2,g3)
    c: Coincident(g3,g0)
    c: Horizontal(g0)
    c: Horizontal(g2)
    c: Vertical(g1)
    c: Vertical(g3)
    c: Coincident(g0,g-4)
    c: PointOnObject(g1,g-3)
    c: DistanceY(g3,g3) = 2.5
FEATURE [PartDesign::Pocket] Pocket
  BaseFeature = -> Pocket001
  Direction = (1,0,0)
  Length = 3
  Length2 = 5
  Profile = -> Sketch004
  ReferenceAxis = -> Sketch004 [N_Axis]
  Refine = true
  SideType = 0
  Suppressed = false
  Type = 0
  Type2 = 0
FEATURE [Sketcher::SketchObject] Sketch005
  ArcFitTolerance = 1e-06
  AttachmentSupport = -> [Pocket]
  ExternalTypes = [0]
  FullyConstrained = true
  MakeInternals = false
  MapMode = 5
  Placement = pos=(5.5,0,0) rot=(0.57735,-0.57735,-0.57735;2.0944rad)
  sketch-geometry (6):
    g0: Circle CenterX=11.5 CenterY=9.25 CenterZ=0 NormalX=0 NormalY=0 NormalZ=1 AngleXU=0 Radius=0.85
    g1: Circle CenterX=8.5 CenterY=9.25 CenterZ=0 NormalX=0 NormalY=0 NormalZ=1 AngleXU=0 Radius=1
    g2: Circle CenterX=11.5 CenterY=-0.25 CenterZ=0 NormalX=0 NormalY=0 NormalZ=1 AngleXU=0 Radius=0.85
    g3: Circle CenterX=8.5 CenterY=-0.25 CenterZ=0 NormalX=0 NormalY=0 NormalZ=1 AngleXU=0 Radius=1
    g4: LineSegment [constr] StartX=11.5 StartY=9.25 StartZ=0 EndX=11.5 EndY=-0.25 EndZ=0
    g5: GeomPoint [constr] X=11.5 Y=4.5 Z=0
  constraints (15):
    c: Diameter(g0) = 1.7
    c: Equal(g2,g0)
    c: DistanceY(g2,g0) = 9.5
    c: Horizontal(g1,g0)
    c: Vertical(g1,g3)
    c: Horizontal(g3,g2)
    c: Equal(g3,g1)
    c: Diameter(g1) = 2
    c: DistanceX(g1,g0) = 3
    c: Vertical(g2,g0)
    c: DistanceX(g-1,g2) = 11.5
    c: Coincident(g4,g0)
    c: Coincident(g4,g2)
    c: Symmetric(g4,g4,g5)
    c: DistanceY(g-1,g5) = 4.5
FEATURE [PartDesign::Pocket] Pocket003
  BaseFeature = -> Pocket
  Direction = (1,0,0)
  Length = 6.5
  Length2 = 5
  Profile = -> Sketch005
  ReferenceAxis = -> Sketch005 [N_Axis]
  Refine = true
  SideType = 0
  Suppressed = false
  Type = 0
  Type2 = 0
FEATURE [PartDesign::PolarPattern] PolarPattern
  Angle = 360
  Axis = -> DatumLine
  BaseFeature = -> Pocket003
  Mode = 0
  Occurrences = 3
  Offset = 120
  Originals = -> [Pocket001,Pocket,Pocket003]
  Refine = true
  SpacingPattern = [0]
  Spacings = [-1,-1]
  Suppressed = false
  TransformMode = 0
FEATURE [PartDesign::Chamfer] Chamfer
  Angle = 45
  Base = -> PolarPattern [Edge11,Edge84,Edge10]
  BaseFeature = -> PolarPattern
  ChamferType = 0
  FlipDirection = false
  Refine = true
  Size = 1
  Size2 = 1
  SupportTransform = false
  Suppressed = false
  UseAllEdges = false
FEATURE [PartDesign::Fillet] Fillet
  Base = -> Chamfer [Edge28,Edge1,Edge42]
  BaseFeature = -> Chamfer
  Radius = 2
  Refine = true
  SupportTransform = false
  Suppressed = false
  UseAllEdges = false
FEATURE [PartDesign::Chamfer] Chamfer001
  Angle = 45
  Base = -> Fillet [Edge41,Edge79,Edge39]
  BaseFeature = -> Fillet
  ChamferType = 0
  FlipDirection = false
  Refine = true
  Size = 0.5
  Size2 = 1
  SupportTransform = false
  Suppressed = false
  UseAllEdges = false
FEATURE [Sketcher::SketchObject] Sketch003
  ArcFitTolerance = 1e-06
  AttachmentSupport = -> [Chamfer001]
  ExternalTypes = [0]
  FullyConstrained = true
  MakeInternals = false
  MapMode = 5
  Placement = pos=(0,0,14.5) rot=(0,0,1;0rad)
  sketch-geometry (3):
    g0: Circle CenterX=6 CenterY=11 CenterZ=0 NormalX=0 NormalY=0 NormalZ=1 AngleXU=0 Radius=1.5
    g1: Circle CenterX=6 CenterY=1 CenterZ=0 NormalX=0 NormalY=0 NormalZ=1 AngleXU=0 Radius=1.5
    g2: LineSegment [constr] StartX=6 StartY=11 StartZ=0 EndX=6 EndY=1 EndZ=0
  constraints (8):
    c: Diameter(g0) = 3
    c: Vertical(g2)
    c: Coincident(g2,g0)
    c: Coincident(g1,g2)
    c: DistanceY(g-1,g0) = 11
    c: DistanceY(g2,g2) = 10
    c: Distance(g-2,g2) = 6
    c: Equal(g1,g0)
FEATURE [PartDesign::Pocket] Pocket002  label="AttachmentHoles"
  BaseFeature = -> Chamfer001
  Direction = (0,0,-1)
  Length = 8
  Length2 = 5
  Profile = -> Sketch003
  ReferenceAxis = -> Sketch003 [N_Axis]
  Refine = true
  SideType = 0
  Suppressed = false
  Type = 0
  Type2 = 0
FEATURE [PartDesign::PolarPattern] PolarPattern001
  Angle = 360
  Axis = -> DatumLine
  BaseFeature = -> Pocket002
  Mode = 0
  Occurrences = 3
  Offset = 120
  Originals = -> [Pocket002]
  Refine = true
  SpacingPattern = [0]
  Spacings = [-1,-1]
  Suppressed = false
  TransformMode = 0
FEATURE [PartDesign::Fillet] Fillet001
  Base = -> PolarPattern001 [Edge4,Edge3,Edge70,Edge71,Edge46,Edge8]
  BaseFeature = -> PolarPattern001
  Radius = 1
  Refine = true
  SupportTransform = false
  Suppressed = false
  UseAllEdges = false
FEATURE [PartDesign::Fillet] Fillet002
  Base = -> Fillet001 [Edge45,Edge22,Edge123]
  BaseFeature = -> Fillet001
  Radius = 2
  Refine = true
  SupportTransform = false
  Suppressed = false
  UseAllEdges = false
FEATURE [Part::DatumPoint] DatumPoint  label="EE_AtachmentPoint0"
  AttacherType = Attacher::AttachEnginePoint
  Placement = pos=(3.54,-11.5,4.5) rot=(0,0,1;0rad)
FEATURE [Part::DatumPoint] DatumPoint001  label="EE_AtachmentPoint1"
  AttacherType = Attacher::AttachEnginePoint
  Placement = pos=(4.5,3.54,-11.5) rot=(0,0,1;0rad)
FEATURE [Part::DatumPoint] DatumPoint002  label="EE_AtachmentPoint2"
  AttacherType = Attacher::AttachEnginePoint
  Placement = pos=(-11.5,4.5,3.54) rot=(0,0,1;0rad)
FEATURE [PartDesign::Body] Body  label="Endeffector"
  AllowCompound = false
  Group = -> [Sketch,Pad,DatumLine,Sketch002,Pocket001,Sketch004,Pocket,Sketch005,Pocket003,PolarPattern,Chamfer,Fillet,Chamfer001,Sketch003,Pocket002,PolarPattern001,Fillet001,Fillet002,DatumPoint,DatumPoint001,DatumPoint002]
  Origin = -> Origin
  Tip = -> Fillet002
FEATURE [Measure::MeasurePosition] Position  label="Position: X: 3.54 mm
Y: -11.50 mm
Z: 4.50 mm"
  Element = -> Body [DatumPoint.]
  Position = (3.54,-11.5,4.5)
FEATURE [Measure::MeasurePosition] Position001  label="Position001: X: 4.50 mm
Y: 3.54 mm
Z: -11.50 mm"
  Element = -> Body [DatumPoint001.]
  Position = (4.5,3.54,-11.5)
FEATURE [Measure::MeasurePosition] Position002  label="Position002: X: -11.50 mm
Y: 4.50 mm
Z: 3.54 mm"
  Element = -> Body [DatumPoint002.]
  Position = (-11.5,4.5,3.54)
FEATURE [App::DocumentObjectGroup] Measurements
  Group = -> [Position,Position001,Position002]
